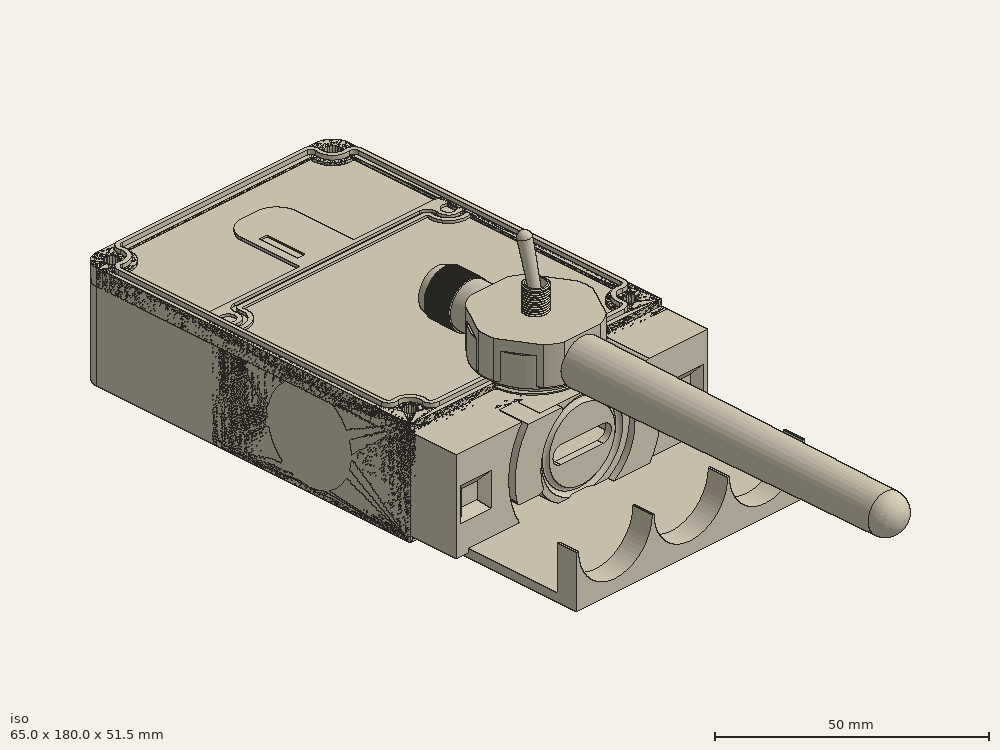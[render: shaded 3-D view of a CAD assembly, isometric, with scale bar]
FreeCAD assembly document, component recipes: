
FREECAD ASSEMBLY — COMPONENT RECIPES ("NomadShell_0.1")

This assembly document has 23 components, labeled P0..P22 below (a component is one placed body or linked part). 12 of them carry a construction recipe — the FreeCAD feature program that regenerates the part from scratch, quoted from this document or its linked companion documents; the rest are supplied as boundary geometry only. No exploded tour is included for this assembly.
NOTE — this tour is split across 2 documents so each fits a 32k-token context. This is document 1: the component sections continue in the remaining 1 document, each repeating the header above.
COMPONENT P0 — geometry summary ("Magnetic Pogo Connector 3 Pin (Type 1)007"; no construction recipe available for this part):
  bounding box: 15.0 x 5.8 x 4.0 mm
  tessellated surface: 7,316 triangles
  volume: 230 mm^3 (67% of its bounding box)
  symmetry: 2-fold rotationally symmetric about the y axis; mirror-symmetric across its x mid-plane, z mid-plane
COMPONENT P1 — geometry summary ("Magnetic Pogo Connector 3 Pin (Type 2)007"; no construction recipe available for this part):
  bounding box: 15.0 x 6.6 x 4.0 mm
  tessellated surface: 8,720 triangles
  volume: 231 mm^3 (58% of its bounding box)
  symmetry: 2-fold rotationally symmetric about the y axis; mirror-symmetric across its x mid-plane, z mid-plane
COMPONENT P2 — geometry summary ("RAK19003 (Solid)001"; no construction recipe available for this part):
  bounding box: 35.8 x 30.0 x 9.4 mm
  tessellated surface: 61,364 triangles
  volume: 1256 mm^3 (12% of its bounding box)
COMPONENT P3 — geometry summary ("RAK4631 (Solid)001"; no construction recipe available for this part):
  bounding box: 30.0 x 20.0 x 4.4 mm
  tessellated surface: 23,072 triangles
  volume: 875 mm^3 (33% of its bounding box)
COMPONENT P4 — geometry summary ("sma001"; no construction recipe available for this part):
  bounding box: 17.0 x 10.2 x 10.2 mm
  tessellated surface: 14,722 triangles
  volume: 428 mm^3 (24% of its bounding box)
COMPONENT P5 — geometry summary ("18650 v003"; no construction recipe available for this part):
  bounding box: 65.0 x 18.0 x 18.0 mm
  tessellated surface: 12,208 triangles
  volume: 16488 mm^3 (78% of its bounding box)
  symmetry: 2-fold rotationally symmetric about the x axis; revolution-symmetric about the y axis through its bounding-box center; 2-fold rotationally symmetric about the z axis; mirror-symmetric across its x mid-plane, y mid-plane, z mid-plane
COMPONENT P6 — geometry summary ("18650 v002"; no construction recipe available for this part):
  bounding box: 65.0 x 18.0 x 18.0 mm
  tessellated surface: 12,208 triangles
  volume: 16488 mm^3 (78% of its bounding box)
  symmetry: 2-fold rotationally symmetric about the x axis; revolution-symmetric about the y axis through its bounding-box center; 2-fold rotationally symmetric about the z axis; mirror-symmetric across its x mid-plane, y mid-plane, z mid-plane
COMPONENT P7 — geometry summary ("antenna_WiFi_RP-SMA_conn v003"; no construction recipe available for this part):
  bounding box: 120.4 x 11.1 x 11.0 mm
  tessellated surface: 27,859 triangles
  volume: 5611 mm^3 (38% of its bounding box)
  symmetry: mirror-symmetric across its x mid-plane
COMPONENT P8 — recipe-attached ("base001", modeled in this document).
Construction recipe (the document's own serialized feature program — sketch geometry with constraints, then the solid features built on it; lengths are millimeters unless a unit is written):

FEATURE [Sketcher::SketchObject] Sketch013  label="main_luge"
  ArcFitTolerance = 1e-06
  AttachmentSupport = -> [XZ_Plane066]
  ExternalTypes = [0]
  FullyConstrained = true
  MakeInternals = false
  MapMode = 5
  Placement = pos=(0,0,0) rot=(1,0,0;1.5708rad)
  expr: Constraints[10] = VarSet.case_height
  expr: Constraints[12] = VarSet.case_height / 2
  expr: Constraints[17] = VarSet.Base_connector_bounting_box_height
  expr: Constraints[29] = VarSet.Base_connector_external_lug
  expr: Constraints[34] = VarSet.Base_connector_external_lug
  expr: Constraints[48] = VarSet.Base_connector_internal_lug
  expr: Constraints[50] = VarSet.Base_connector_internal_lug
  expr: Constraints[52] = VarSet.Base_connector_lug_remaining_key
  expr: Constraints[53] = VarSet.Base_connector_lug_remaining_key
  expr: Constraints[9] = VarSet.base_width
  sketch-geometry (20):
    g0: LineSegment [constr] StartX=-32.5 StartY=0 StartZ=0 EndX=-32.5 EndY=-25 EndZ=0
    g1: LineSegment [constr] StartX=-32.5 StartY=-25 StartZ=0 EndX=32.5 EndY=-25 EndZ=0
    g2: LineSegment [constr] StartX=32.5 StartY=-25 StartZ=0 EndX=32.5 EndY=0 EndZ=0
    g3: LineSegment [constr] StartX=32.5 StartY=0 StartZ=0 EndX=-32.5 EndY=0 EndZ=0
    g4: GeomPoint X=0 Y=-12.5 Z=0
    g5: LineSegment [constr] StartX=-32.5 StartY=-1.5 StartZ=0 EndX=32.5 EndY=-1.5 EndZ=0
    g6: LineSegment [constr] StartX=-32.5 StartY=-23.5 StartZ=0 EndX=32.5 EndY=-23.5 EndZ=0
    g7: LineSegment [constr] StartX=-32.5 StartY=-1.5 StartZ=0 EndX=32.5 EndY=-23.5 EndZ=0
    g8: ArcOfCircle CenterX=0 CenterY=-12.5 CenterZ=0 NormalX=0 NormalY=0 NormalZ=1 AngleXU=0 Radius=12 StartAngle=5.85341 EndAngle=7.44284
    g9: ArcOfCircle CenterX=0 CenterY=-12.5 CenterZ=0 NormalX=0 NormalY=0 NormalZ=1 AngleXU=0 Radius=19 StartAngle=6.01689 EndAngle=6.90062
    g10: LineSegment StartX=10.9087 StartY=-17.5 StartZ=0 EndX=18.3303 EndY=-17.5 EndZ=0
    g11: LineSegment StartX=4.79583 StartY=-1.5 StartZ=0 EndX=15.4919 EndY=-1.5 EndZ=0
    g12: ArcOfCircle CenterX=0 CenterY=-12.5 CenterZ=0 NormalX=0 NormalY=0 NormalZ=1 AngleXU=0 Radius=12 StartAngle=2.71182 EndAngle=4.30125
    g13: ArcOfCircle CenterX=0 CenterY=-12.5 CenterZ=0 NormalX=0 NormalY=0 NormalZ=1 AngleXU=0 Radius=19 StartAngle=2.8753 EndAngle=3.75903
    g14: LineSegment StartX=-18.3303 StartY=-7.5 StartZ=0 EndX=-10.9087 EndY=-7.5 EndZ=0
    g15: LineSegment StartX=-15.4919 StartY=-23.5 StartZ=0 EndX=-4.79583 EndY=-23.5 EndZ=0
    g16: LineSegment StartX=-32.5 StartY=-1.5 StartZ=0 EndX=-32.5 EndY=-23.5 EndZ=0
    g17: LineSegment StartX=-32.5 StartY=-23.5 StartZ=0 EndX=32.5 EndY=-23.5 EndZ=0
    g18: LineSegment StartX=32.5 StartY=-23.5 StartZ=0 EndX=32.5 EndY=-1.5 EndZ=0
    g19: LineSegment StartX=32.5 StartY=-1.5 StartZ=0 EndX=-32.5 EndY=-1.5 EndZ=0
  constraints (56):
    c: Coincident(g0,g1)
    c: Coincident(g1,g2)
    c: Coincident(g2,g3)
    c: Coincident(g3,g0)
    c: Vertical(g0)
    c: Vertical(g2)
    c: Horizontal(g1)
    c: PointOnObject(g0,g-1)
    c: Symmetric(g0,g2,g-2)
    c: DistanceX(g0,g2) = 65
    c: DistanceY(g0,g-1) = 25
    c: PointOnObject(g4,g-2)
    c: DistanceY(g4,g-1) = 12.5
    c: PointOnObject(g6,g0)
    c: Horizontal(g6)
    c: PointOnObject(g6,g2)
    c: PointOnObject(g5,g2)
    c: DistanceY(g6,g5) = 22
    c: PointOnObject(g5,g0)
    c: Parallel(g5,g3)
    c: Coincident(g7,g5)
    c: Coincident(g7,g6)
    c: PointOnObject(g4,g7)
    c: Coincident(g8,g4)
    c: Coincident(g9,g4)
    c: Coincident(g10,g8)
    c: Coincident(g10,g9)
    c: Coincident(g9,g11)
    c: Parallel(g11,g3)
    c: Radius(g9) = 19
    c: Coincident(g12,g4)
    c: Coincident(g13,g4)
    c: Coincident(g14,g13)
    c: Coincident(g14,g12)
    c: Radius(g13) = 19
    c: Coincident(g15,g13)
    c: Parallel(g15,g5)
    c: Coincident(g16,g17)
    c: Coincident(g17,g18)
    c: Coincident(g18,g19)
    c: Coincident(g19,g16)
    c: Vertical(g16)
    c: Horizontal(g17)
    c: Symmetric(g16,g18,g-2)
    c: Parallel(g10,g5)
    c: Parallel(g14,g5)
    c: Coincident(g16,g5)
    c: Coincident(g17,g6)
    c: Radius(g12) = 12
    c: PointOnObject(g12,g6)
    c: Radius(g8) = 12
    c: PointOnObject(g8,g5)
    c: Distance(g9,g17) = 6
    c: Distance(g12,g19) = 6
    c: Coincident(g11,g8)
    c: Coincident(g15,g12)
FEATURE [Sketcher::SketchObject] Sketch014
  ArcFitTolerance = 1e-06
  AttachmentSupport = -> [XZ_Plane066]
  ExternalTypes = [0]
  FullyConstrained = true
  MakeInternals = false
  MapMode = 5
  Placement = pos=(0,0,0) rot=(1,0,0;1.5708rad)
  expr: Constraints[11] = VarSet.Base_connector_bounting_box_height
  expr: Constraints[18] = (VarSet.Base_connector_external_lug + VarSet.Base_connector_internal_lug) / 2
  expr: Constraints[19] = (VarSet.Base_connector_external_lug + VarSet.Base_connector_internal_lug) / 2
  expr: Constraints[24] = VarSet.Base_connector_internal_lug
  expr: Constraints[28] = VarSet.Base_connector_internal_lug
  expr: Constraints[36] = VarSet.Base_connector_bounting_box_height - VarSet.Base_connector_height_lug
  expr: Constraints[38] = VarSet.Base_connector_bounting_box_height - VarSet.Base_connector_height_lug
  expr: Constraints[3] = VarSet.base_width
  expr: Constraints[6] = VarSet.case_height / 2
  sketch-geometry (14):
    g0: LineSegment [constr] StartX=-32.5 StartY=-1.5 StartZ=0 EndX=-32.5 EndY=-23.5 EndZ=0
    g1: LineSegment [constr] StartX=-32.5 StartY=-23.5 StartZ=0 EndX=32.5 EndY=-23.5 EndZ=0
    g2: LineSegment [constr] StartX=32.5 StartY=-23.5 StartZ=0 EndX=32.5 EndY=-1.5 EndZ=0
    g3: GeomPoint X=0 Y=-12.5 Z=0
    g4: LineSegment [constr] StartX=-32.5 StartY=-12.5 StartZ=0 EndX=32.5 EndY=-12.5 EndZ=0
    g5: LineSegment StartX=11.9583 StartY=-13.5 StartZ=0 EndX=15.4677 EndY=-13.5 EndZ=0
    g6: LineSegment [constr] StartX=-32.5 StartY=-1.5 StartZ=0 EndX=32.5 EndY=-1.5 EndZ=0
    g7: ArcOfCircle CenterX=0 CenterY=-12.5 CenterZ=0 NormalX=0 NormalY=0 NormalZ=1 AngleXU=0 Radius=15.5 StartAngle=6.21862 EndAngle=7.07223
    g8: ArcOfCircle CenterX=-1.6e-15 CenterY=-12.5 CenterZ=0 NormalX=0 NormalY=0 NormalZ=1 AngleXU=0 Radius=15.5 StartAngle=3.07703 EndAngle=3.93063
    g9: LineSegment StartX=-15.4677 StartY=-11.5 StartZ=0 EndX=-11.9583 EndY=-11.5 EndZ=0
    g10: ArcOfCircle CenterX=-1.6e-15 CenterY=-12.5 CenterZ=0 NormalX=0 NormalY=0 NormalZ=1 AngleXU=0 Radius=12 StartAngle=3.05816 EndAngle=4.30125
    g11: LineSegment StartX=-4.79583 StartY=-23.5 StartZ=0 EndX=-10.9202 EndY=-23.5 EndZ=0
    g12: ArcOfCircle CenterX=0 CenterY=-12.5 CenterZ=0 NormalX=0 NormalY=0 NormalZ=1 AngleXU=0 Radius=12 StartAngle=6.19976 EndAngle=7.44284
    g13: LineSegment StartX=4.79583 StartY=-1.5 StartZ=0 EndX=10.9202 EndY=-1.5 EndZ=0
  constraints (39):
    c: Vertical(g0)
    c: Vertical(g2)
    c: Horizontal(g1)
    c: DistanceX(g0,g2) = 65
    c: Symmetric(g0,g2,g-2)
    c: PointOnObject(g3,g-2)
    c: DistanceY(g3,g-1) = 12.5
    c: Symmetric(g0,g0,g4)
    c: Symmetric(g2,g2,g4)
    c: Coincident(g1,g2)
    c: Coincident(g1,g0)
    c: DistanceY(g1,g2) = 22
    c: Coincident(g6,g0)
    c: Coincident(g6,g2)
    c: PointOnObject(g3,g4)
    c: Coincident(g7,g3)
    c: Coincident(g7,g5)
    c: Symmetric(g4,g4,g8)
    c: Radius(g7) = 15.5
    c: Radius(g8) = 15.5
    c: Coincident(g8,g9)
    c: Coincident(g10,g8)
    c: Coincident(g10,g9)
    c: Coincident(g11,g10)
    c: Radius(g10) = 12
    c: Coincident(g8,g11)
    c: Coincident(g12,g3)
    c: Coincident(g12,g5)
    c: Radius(g12) = 12
    c: Coincident(g13,g12)
    c: Coincident(g13,g7)
    c: Parallel(g9,g6)
    c: Parallel(g1,g5)
    c: Parallel(g11,g1)
    c: Parallel(g13,g1)
    c: PointOnObject(g10,g1)
    c: Distance(g8,g6) = 10
    c: PointOnObject(g7,g6)
    c: Distance(g5,g1) = 10
FEATURE [PartDesign::Pad] Pad010
  Direction = (0,-1,2e-16)
  Length = 12
  Length2 = 10
  Placement = pos=(0,0,0) rot=(1,0,0;1.5708rad)
  Profile = -> Sketch013 [Edge9,Edge12,Edge10,Edge11]
  ReferenceAxis = -> Sketch013 [N_Axis]
  Refine = true
  Suppressed = false
  Type = 0
  expr: Length = VarSet.Base_connector_height_lug
FEATURE [PartDesign::Pocket] Pocket021
  BaseFeature = -> Pad010
  Direction = (0,1,-2e-16)
  Length = 6.2
  Length2 = 5
  Placement = pos=(0,0,0) rot=(1,0,0;1.5708rad)
  Profile = -> Sketch013 [Edge7,Edge8,Edge6,Edge5,Edge3,Edge2,Edge4,Edge1]
  ReferenceAxis = -> Sketch013 [N_Axis]
  Refine = true
  Reversed = true
  Suppressed = false
  Type = 0
  expr: Length = VarSet.Base_connector_height_lug / 2 + VarSet.Base_connector_oring_offset
FEATURE [Sketcher::SketchObject] Sketch016
  ArcFitTolerance = 1e-06
  AttachmentSupport = -> [Pocket021]
  ExternalTypes = [0]
  FullyConstrained = false
  MakeInternals = false
  MapMode = 5
  Placement = pos=(0,-12,0) rot=(1,0,0;1.5708rad)
  expr: Constraints[11] = VarSet.Base_connector_bounting_box_height
  expr: Constraints[17] = VarSet.Base_connector_external_lug
  expr: Constraints[18] = 19
  expr: Constraints[20] = VarSet.Base_connector_internal_lug
  expr: Constraints[28] = (VarSet.Base_connector_external_lug + VarSet.Base_connector_internal_lug) / 2
  expr: Constraints[39] = VarSet.Base_connector_lug_remaining_key
  expr: Constraints[3] = VarSet.base_width
  expr: Constraints[47] = (VarSet.Base_connector_external_lug + VarSet.Base_connector_internal_lug) / 2
  expr: Constraints[48] = VarSet.Base_connector_internal_lug
  expr: Constraints[54] = VarSet.Base_connector_lug_remaining_key
  expr: Constraints[6] = VarSet.case_height / 2
  sketch-geometry (20):
    g0: LineSegment [constr] StartX=-32.5 StartY=-1.5 StartZ=0 EndX=-32.5 EndY=-23.5 EndZ=0
    g1: LineSegment [constr] StartX=-32.5 StartY=-23.5 StartZ=0 EndX=32.5 EndY=-23.5 EndZ=0
    g2: LineSegment [constr] StartX=32.5 StartY=-23.5 StartZ=0 EndX=32.5 EndY=-1.5 EndZ=0
    g3: GeomPoint X=0 Y=-12.5 Z=0
    g4: LineSegment [constr] StartX=-32.5 StartY=-12.5 StartZ=0 EndX=32.5 EndY=-12.5 EndZ=0
    g5: LineSegment [constr] StartX=-32.5 StartY=-1.5 StartZ=0 EndX=32.5 EndY=-1.5 EndZ=0
    g6: ArcOfCircle CenterX=0 CenterY=-12.5 CenterZ=0 NormalX=0 NormalY=0 NormalZ=1 AngleXU=0 Radius=19 StartAngle=5.66575 EndAngle=6.90062
    g7: ArcOfCircle CenterX=-3e-16 CenterY=-12.5 CenterZ=0 NormalX=0 NormalY=0 NormalZ=1 AngleXU=0 Radius=19 StartAngle=2.52416 EndAngle=3.75903
    g8: ArcOfCircle CenterX=0 CenterY=-12.5 CenterZ=0 NormalX=0 NormalY=0 NormalZ=1 AngleXU=0 Radius=12 StartAngle=0.429775 EndAngle=1.15966
    g9: ArcOfCircle CenterX=0 CenterY=-12.5 CenterZ=0 NormalX=0 NormalY=0 NormalZ=1 AngleXU=0 Radius=15.5 StartAngle=5.49415 EndAngle=6.61164
    g10: LineSegment [constr] StartX=-15.4919 StartY=-1.5 StartZ=0 EndX=-4.79582 EndY=-1.5 EndZ=0
    g11: LineSegment [constr] StartX=-13.0749 StartY=-23.5 StartZ=0 EndX=-4.79583 EndY=-23.5 EndZ=0
    g12: LineSegment StartX=15.4919 StartY=-1.5 StartZ=0 EndX=4.79583 EndY=-1.5 EndZ=0
    g13: LineSegment StartX=15.4919 StartY=-23.5 StartZ=0 EndX=10.9202 EndY=-23.5 EndZ=0
    g14: LineSegment StartX=14.6714 StartY=-7.5 StartZ=0 EndX=10.9087 EndY=-7.5 EndZ=0
    g15: LineSegment StartX=-15.4919 StartY=-23.5 StartZ=0 EndX=-4.79583 EndY=-23.5 EndZ=0
    g16: LineSegment StartX=-10.9202 StartY=-1.5 StartZ=0 EndX=-15.4919 EndY=-1.5 EndZ=0
    g17: LineSegment StartX=-14.6714 StartY=-17.5 StartZ=0 EndX=-10.9087 EndY=-17.5 EndZ=0
    g18: ArcOfCircle CenterX=-3e-16 CenterY=-12.5 CenterZ=0 NormalX=0 NormalY=0 NormalZ=1 AngleXU=0 Radius=15.5 StartAngle=2.35255 EndAngle=3.47005
    g19: ArcOfCircle CenterX=0 CenterY=-12.5 CenterZ=0 NormalX=0 NormalY=0 NormalZ=1 AngleXU=0 Radius=12 StartAngle=3.57137 EndAngle=4.30125
  constraints (55):
    c: Vertical(g0)
    c: Vertical(g2)
    c: Horizontal(g1)
    c: DistanceX(g0,g2) = 65
    c: Symmetric(g0,g2,g-2)
    c: PointOnObject(g3,g-2)
    c: DistanceY(g3,g-1) = 12.5
    c: Symmetric(g0,g0,g4)
    c: Symmetric(g2,g2,g4)
    c: Coincident(g1,g2)
    c: Coincident(g1,g0)
    c: DistanceY(g1,g2) = 22
    c: Coincident(g5,g0)
    c: Coincident(g5,g2)
    c: PointOnObject(g3,g4)
    c: Coincident(g6,g3)
    c: Symmetric(g4,g4,g7)
    c: Radius(g6) = 19
    c: Radius(g7) = 19
    c: Coincident(g8,g3)
    c: Radius(g8) = 12
    c: Coincident(g9,g3)
    c: PointOnObject(g8,g5)
    c: PointOnObject(g10,g5)
    c: PointOnObject(g11,g1)
    c: PointOnObject(g7,g5)
    c: Coincident(g10,g7)
    c: PointOnObject(g11,g1)
    c: Radius(g9) = 15.5
    c: PointOnObject(g6,g5)
    c: Coincident(g12,g6)
    c: Coincident(g12,g8)
    c: PointOnObject(g6,g1)
    c: Coincident(g13,g9)
    c: Horizontal(g13)
    c: Coincident(g14,g9)
    c: Parallel(g14,g5)
    c: Coincident(g14,g8)
    c: Coincident(g13,g6)
    c: Distance(g8,g5) = 6
    c: Coincident(g16,g7)
    c: Horizontal(g17)
    c: PointOnObject(g16,g5)
    c: Coincident(g18,g7)
    c: Coincident(g18,g16)
    c: Coincident(g19,g3)
    c: Coincident(g19,g15)
    c: Radius(g18) = 15.5
    c: Radius(g19) = 12
    c: Coincident(g17,g19)
    c: Coincident(g17,g18)
    c: Coincident(g7,g15)
    c: PointOnObject(g7,g1)
    c: PointOnObject(g15,g1)
    c: Distance(g7,g17) = 6
FEATURE [PartDesign::Pocket] Pocket022
  BaseFeature = -> Pocket021
  Direction = (0,1,-2e-16)
  Length = 6
  Length2 = 5
  Placement = pos=(0,0,0) rot=(1,0,0;1.5708rad)
  Profile = -> Sketch016
  ReferenceAxis = -> Sketch016 [N_Axis]
  Refine = true
  Suppressed = false
  Type = 0
  expr: Length = VarSet.Base_connector_height_lug / 2
FEATURE [Sketcher::SketchObject] Sketch017  label="pogo_pins001"
  ArcFitTolerance = 1e-06
  AttachmentSupport = -> [Pocket022]
  ExternalTypes = [0]
  FullyConstrained = true
  MakeInternals = false
  MapMode = 5
  Placement = pos=(0,-12,0) rot=(1,0,0;1.5708rad)
  expr: Constraints[12] = VarSet.Base_pogopins_r
  expr: Constraints[1] = VarSet.case_height / 2
  expr: Constraints[25] = VarSet.Base_pogoping_lenght
  sketch-geometry (11):
    g0: GeomPoint X=0 Y=-12.5 Z=0
    g1: ArcOfCircle CenterX=-5.45 CenterY=-12.5 CenterZ=0 NormalX=0 NormalY=0 NormalZ=1 AngleXU=0 Radius=2.1 StartAngle=1.5708 EndAngle=4.71239
    g2: ArcOfCircle CenterX=5.45 CenterY=-12.5 CenterZ=0 NormalX=0 NormalY=0 NormalZ=1 AngleXU=0 Radius=2.1 StartAngle=4.71239 EndAngle=7.85398
    g3: LineSegment StartX=-5.45 StartY=-10.4 StartZ=0 EndX=5.45 EndY=-10.4 EndZ=0
    g4: LineSegment StartX=-5.45 StartY=-14.6 StartZ=0 EndX=5.45 EndY=-14.6 EndZ=0
    g5: LineSegment [constr] StartX=-5.45 StartY=-12.5 StartZ=0 EndX=5.45 EndY=-12.5 EndZ=0
    g6: GeomPoint [constr] X=0 Y=-12.5 Z=0
    g7: LineSegment [constr] StartX=-7.55 StartY=-10.4 StartZ=0 EndX=-7.55 EndY=-14.6 EndZ=0
    g8: LineSegment [constr] StartX=-7.55 StartY=-14.6 StartZ=0 EndX=7.55 EndY=-14.6 EndZ=0
    g9: LineSegment [constr] StartX=7.55 StartY=-14.6 StartZ=0 EndX=7.55 EndY=-10.4 EndZ=0
    g10: LineSegment [constr] StartX=7.55 StartY=-10.4 StartZ=0 EndX=-7.55 EndY=-10.4 EndZ=0
  constraints (26):
    c: PointOnObject(g0,g-2)
    c: Distance(g0,g-1) = 12.5
    c: Tangent(g1,g3) = 1.5708
    c: Tangent(g1,g4) = -1.5708
    c: Tangent(g2,g3) = 1.5708
    c: Tangent(g2,g4) = -1.5708
    c: Equal(g1,g2)
    c: Horizontal(g3)
    c: Coincident(g5,g1)
    c: Coincident(g5,g2)
    c: Symmetric(g5,g5,g6)
    c: Coincident(g0,g6)
    c: Radius(g1) = 2.1
    c: Coincident(g7,g8)
    c: Coincident(g8,g9)
    c: Coincident(g9,g10)
    c: Coincident(g10,g7)
    c: Vertical(g7)
    c: Vertical(g9)
    c: Horizontal(g8)
    c: Horizontal(g10)
    c: PointOnObject(g2,g10)
    c: PointOnObject(g2,g8)
    c: Tangent(g2,g9)
    c: Tangent(g7,g1)
    c: DistanceX(g7,g9) = 15.1
FEATURE [PartDesign::Pocket] Pocket023  label="pogo_pins002"
  BaseFeature = -> Pocket022
  Direction = (0,1,-2e-16)
  Length = 1.5
  Length2 = 5
  Placement = pos=(0,0,0) rot=(1,0,0;1.5708rad)
  Profile = -> Sketch017
  ReferenceAxis = -> Sketch017 [N_Axis]
  Refine = true
  Suppressed = false
  Type = 0
  expr: Length = VarSet.Base_pogopin_cutout_height
FEATURE [Sketcher::SketchObject] Sketch023  label="pogo_pins_outside"
  ArcFitTolerance = 1e-06
  AttachmentSupport = -> [XZ_Plane066]
  ExternalTypes = [0]
  FullyConstrained = true
  MakeInternals = false
  MapMode = 5
  Placement = pos=(0,0,0) rot=(1,0,0;1.5708rad)
  expr: Constraints[12] = VarSet.Base_pogopin_outside
  expr: Constraints[13] = VarSet.Base_pogopins_r * 3
  expr: Constraints[1] = VarSet.case_height / 2
  sketch-geometry (6):
    g0: GeomPoint X=0 Y=-12.5 Z=0
    g1: LineSegment StartX=-10.5 StartY=-9.35 StartZ=0 EndX=-10.5 EndY=-15.65 EndZ=0
    g2: LineSegment StartX=-10.5 StartY=-15.65 StartZ=0 EndX=10.5 EndY=-15.65 EndZ=0
    g3: LineSegment StartX=10.5 StartY=-15.65 StartZ=0 EndX=10.5 EndY=-9.35 EndZ=0
    g4: LineSegment StartX=10.5 StartY=-9.35 StartZ=0 EndX=-10.5 EndY=-9.35 EndZ=0
    g5: GeomPoint [constr] X=0 Y=-12.5 Z=0
  constraints (14):
    c: PointOnObject(g0,g-2)
    c: DistanceY(g0,g-1) = 12.5
    c: Coincident(g1,g2)
    c: Coincident(g2,g3)
    c: Coincident(g3,g4)
    c: Coincident(g4,g1)
    c: Vertical(g1)
    c: Vertical(g3)
    c: Horizontal(g2)
    c: Horizontal(g4)
    c: Symmetric(g3,g1,g5)
    c: Coincident(g5,g0)
    c: Distance(g1,g3) = 21
    c: DistanceY(g2,g3) = 6.3
FEATURE [PartDesign::Pocket] Pocket024  label="pogo_pins_outside001"
  BaseFeature = -> Pocket023
  Direction = (0,1,-2e-16)
  Length = 10.5
  Length2 = 5
  Placement = pos=(0,0,0) rot=(1,0,0;1.5708rad)
  Profile = -> Sketch023
  ReferenceAxis = -> Sketch023 [N_Axis]
  Refine = true
  Reversed = true
  Suppressed = false
  Type = 0
  expr: Length = VarSet.Base_connector_height_lug - VarSet.Base_pogopin_cutout_height
FEATURE [PartDesign::Fillet] Fillet
  Base = -> Pocket024 [Edge5,Edge60]
  BaseFeature = -> Pocket024
  Placement = pos=(0,0,0) rot=(1,0,0;1.5708rad)
  Radius = 10
  Refine = true
  SupportTransform = false
  Suppressed = false
  UseAllEdges = false
FEATURE [Sketcher::SketchObject] Sketch  label="main_diamention"
  ArcFitTolerance = 1e-06
  AttachmentSupport = -> [XY_Plane053]
  ExternalTypes = [0]
  FullyConstrained = true
  MakeInternals = false
  MapMode = 5
  expr: Constraints[13] = VarSet.base_width
  expr: Constraints[14] = VarSet.Base_base_lenght
  expr: Constraints[30] = VarSet.Base_m3_insert
  expr: Constraints[45] = VarSet.Base_case_thickness
  expr: Constraints[46] = VarSet.Base_case_thickness
  expr: Constraints[47] = VarSet.Base_case_thickness
  expr: Constraints[50] = VarSet.Base_case_thickness + VarSet.Base_m3_insert / 2
  expr: Constraints[51] = VarSet.Base_case_thickness + VarSet.Base_m3_insert / 2
  expr: Constraints[52] = VarSet.Base_case_thickness + VarSet.Base_m3_insert / 2
  expr: Constraints[71] = VarSet.Base_case_thickness / 2
  expr: Constraints[72] = VarSet.Base_case_thickness / 2
  expr: Constraints[73] = VarSet.Base_case_thickness / 2
  expr: Constraints[84] = VarSet.Base_case_thickness / 2
  expr: Constraints[86] = VarSet.Base_case_thickness + VarSet.Base_m3_insert / 2
  expr: Constraints[92] = VarSet.Base_case_thickness
  sketch-geometry (40):
    g0: LineSegment StartX=-32.5 StartY=0 StartZ=0 EndX=32.5 EndY=0 EndZ=0
    g1: LineSegment StartX=32.5 StartY=0 StartZ=0 EndX=32.5 EndY=51 EndZ=0
    g2: LineSegment StartX=28.5 StartY=55 StartZ=0 EndX=-28.5 EndY=55 EndZ=0
    g3: LineSegment StartX=-32.5 StartY=51 StartZ=0 EndX=-32.5 EndY=0 EndZ=0
    g4: GeomPoint [constr] X=-32.5 Y=55 Z=0
    g5: ArcOfCircle CenterX=28.5 CenterY=51 CenterZ=0 NormalX=0 NormalY=0 NormalZ=1 AngleXU=0 Radius=4 StartAngle=0 EndAngle=1.5708
    g6: GeomPoint [constr] X=32.5 Y=55 Z=0
    g7: Circle CenterX=-28.5 CenterY=4 CenterZ=0 NormalX=0 NormalY=0 NormalZ=1 AngleXU=0 Radius=1.6
    g8: Circle CenterX=28.5 CenterY=4 CenterZ=0 NormalX=0 NormalY=0 NormalZ=1 AngleXU=0 Radius=1.6
    g9: Circle CenterX=28.5 CenterY=51 CenterZ=0 NormalX=0 NormalY=0 NormalZ=1 AngleXU=0 Radius=1.6
    g10: Circle CenterX=-28.5 CenterY=51 CenterZ=0 NormalX=0 NormalY=0 NormalZ=1 AngleXU=0 Radius=1.6
    g11: LineSegment [constr] StartX=-28.5 StartY=51 StartZ=0 EndX=-28.5 EndY=4 EndZ=0
    g12: LineSegment [constr] StartX=-28.5 StartY=4 StartZ=0 EndX=28.5 EndY=4 EndZ=0
    g13: LineSegment [constr] StartX=28.5 StartY=4 StartZ=0 EndX=28.5 EndY=51 EndZ=0
    g14: LineSegment [constr] StartX=28.5 StartY=51 StartZ=0 EndX=-28.5 EndY=51 EndZ=0
    g15: LineSegment StartX=-24.01 StartY=52 StartZ=0 EndX=24.01 EndY=52 EndZ=0
    g16: LineSegment StartX=29.5 StartY=46.51 StartZ=0 EndX=29.5 EndY=8.48999 EndZ=0
    g17: LineSegment StartX=24.01 StartY=3 StartZ=0 EndX=-24.01 EndY=3 EndZ=0
    g18: LineSegment StartX=-29.5 StartY=8.48999 StartZ=0 EndX=-29.5 EndY=46.51 EndZ=0
    g19: ArcOfCircle CenterX=-28.5 CenterY=4 CenterZ=0 NormalX=0 NormalY=0 NormalZ=1 AngleXU=0 Radius=4.6 StartAngle=6.06404 EndAngle=8.07312
    g20: ArcOfCircle CenterX=-28.5 CenterY=51 CenterZ=0 NormalX=0 NormalY=0 NormalZ=1 AngleXU=0 Radius=4.6 StartAngle=4.49325 EndAngle=6.50233
    g21: ArcOfCircle CenterX=28.5 CenterY=51 CenterZ=0 NormalX=0 NormalY=0 NormalZ=1 AngleXU=0 Radius=4.6 StartAngle=2.92245 EndAngle=4.93153
    g22: ArcOfCircle CenterX=28.5 CenterY=4 CenterZ=0 NormalX=0 NormalY=0 NormalZ=1 AngleXU=0 Radius=4.6 StartAngle=1.35166 EndAngle=3.36073
    g23: ArcOfCircle CenterX=28.5 CenterY=4 CenterZ=0 NormalX=0 NormalY=0 NormalZ=1 AngleXU=0 Radius=3.1 StartAngle=1.35166 EndAngle=3.36073
    g24: ArcOfCircle CenterX=24.01 CenterY=3 CenterZ=0 NormalX=0 NormalY=0 NormalZ=1 AngleXU=-3.14159 Radius=1.5 StartAngle=1.5708 EndAngle=3.36073
    g25: LineSegment StartX=24.01 StartY=1.5 StartZ=0 EndX=-24.01 EndY=1.5 EndZ=0
    g26: ArcOfCircle CenterX=-24.01 CenterY=3 CenterZ=0 NormalX=0 NormalY=0 NormalZ=1 AngleXU=1.55119 Radius=1.5 StartAngle=1.37126 EndAngle=3.1612
    g27: ArcOfCircle CenterX=-28.5 CenterY=4 CenterZ=0 NormalX=0 NormalY=0 NormalZ=1 AngleXU=0 Radius=3.1 StartAngle=6.06404 EndAngle=8.07312
    g28: ArcOfCircle CenterX=-29.5 CenterY=8.48999 CenterZ=0 NormalX=0 NormalY=0 NormalZ=1 AngleXU=1.5708 Radius=1.5 StartAngle=1.5708 EndAngle=3.36073
    g29: LineSegment StartX=-31 StartY=8.48999 StartZ=0 EndX=-31 EndY=46.51 EndZ=0
    g30: ArcOfCircle CenterX=-29.5 CenterY=46.51 CenterZ=0 NormalX=0 NormalY=0 NormalZ=1 AngleXU=-0.0196091 Radius=1.5 StartAngle=1.37126 EndAngle=3.1612
    g31: ArcOfCircle CenterX=-28.5 CenterY=51 CenterZ=0 NormalX=0 NormalY=0 NormalZ=1 AngleXU=0 Radius=3.1 StartAngle=4.49325 EndAngle=6.50233
    g32: ArcOfCircle CenterX=-24.01 CenterY=52 CenterZ=0 NormalX=0 NormalY=0 NormalZ=1 AngleXU=0 Radius=1.5 StartAngle=1.5708 EndAngle=3.36073
    g33: LineSegment StartX=-24.01 StartY=53.5 StartZ=0 EndX=24.01 EndY=53.5 EndZ=0
    g34: ArcOfCircle CenterX=24.01 CenterY=52 CenterZ=0 NormalX=0 NormalY=0 NormalZ=1 AngleXU=-1.5708 Radius=1.5 StartAngle=1.35166 EndAngle=3.14159
    g35: ArcOfCircle CenterX=28.5 CenterY=51 CenterZ=0 NormalX=0 NormalY=0 NormalZ=1 AngleXU=0 Radius=3.1 StartAngle=2.92245 EndAngle=4.93153
    g36: ArcOfCircle CenterX=29.5 CenterY=46.51 CenterZ=0 NormalX=0 NormalY=0 NormalZ=1 AngleXU=-1.5708 Radius=1.5 StartAngle=1.5708 EndAngle=3.36073
    g37: LineSegment StartX=31 StartY=46.51 StartZ=0 EndX=31 EndY=8.48999 EndZ=0
    g38: ArcOfCircle CenterX=29.5 CenterY=8.48999 CenterZ=0 NormalX=0 NormalY=0 NormalZ=1 AngleXU=3.12198 Radius=1.5 StartAngle=1.37126 EndAngle=3.1612
    g39: ArcOfCircle CenterX=-28.5 CenterY=51 CenterZ=0 NormalX=0 NormalY=0 NormalZ=1 AngleXU=0 Radius=4 StartAngle=1.5708 EndAngle=3.14159
  constraints (94):
    c: Coincident(g0,g1)
    c: Coincident(g3,g0)
    c: Horizontal(g2)
    c: Vertical(g1)
    c: Vertical(g3)
    c: PointOnObject(g0,g-1)
    c: Symmetric(g0,g0,g-2)
    c: PointOnObject(g4,g3)
    c: PointOnObject(g4,g2)
    c: PointOnObject(g6,g1)
    c: PointOnObject(g6,g2)
    c: Tangent(g1,g5) = -1.5708
    c: Tangent(g2,g5) = -1.5708
    c: DistanceX(g4,g6) = 65
    c: DistanceY(g0,g4) = 55
    c: Coincident(g11,g12)
    c: Coincident(g12,g13)
    c: Coincident(g13,g14)
    c: Coincident(g14,g11)
    c: Vertical(g11)
    c: Vertical(g13)
    c: Horizontal(g12)
    c: Coincident(g11,g10)
    c: Coincident(g12,g8)
    c: Coincident(g7,g11)
    c: Coincident(g13,g9)
    c: Symmetric(g10,g9,g-2)
    c: Equal(g10,g9)
    c: Equal(g9,g8)
    c: Equal(g8,g7)
    c: Diameter(g10) = 3.2
    c: Distance(g10,g2) = 2.4
    c: Distance(g7,g0) = 2.4
    c: Horizontal(g15)
    c: Vertical(g16)
    c: Horizontal(g17)
    c: Vertical(g18)
    c: Coincident(g19,g18)
    c: Coincident(g19,g17)
    c: Coincident(g20,g18)
    c: Coincident(g20,g15)
    c: Coincident(g21,g15)
    c: Coincident(g21,g16)
    c: Coincident(g22,g16)
    c: Coincident(g22,g17)
    c: Distance(g2,g15) = 3
    c: Distance(g17,g0) = 3
    c: Distance(g1,g16) = 3
    c: Coincident(g22,g8)
    c: Coincident(g19,g7)
    c: Radius(g19) = 4.6
    c: Radius(g20) = 4.6
    c: Radius(g21) = 4.6
    c: Coincident(g10,g20)
    c: Coincident(g21,g5)
    c: Tangent(g23,g24) = 1.5708
    c: Tangent(g23,g38) = 1.5708
    c: Tangent(g24,g25) = 1.5708
    c: Tangent(g25,g26) = 1.5708
    c: Tangent(g26,g27) = 1.5708
    c: Tangent(g27,g28) = 1.5708
    c: Tangent(g28,g29) = 1.5708
    c: Tangent(g29,g30) = 1.5708
    c: Tangent(g30,g31) = 1.5708
    c: Tangent(g31,g32) = 1.5708
    c: Tangent(g32,g33) = 1.5708
    c: Tangent(g33,g34) = 1.5708
    c: Tangent(g34,g35) = 1.5708
    c: Tangent(g35,g36) = 1.5708
    c: Tangent(g36,g37) = 1.5708
    c: Tangent(g37,g38) = 1.5708
    c: Distance(g17,g25) = 1.5
    c: Distance(g37,g16) = 1.5
    c: Distance(g33,g15) = 1.5
    c: Coincident(g32,g15)
    c: Coincident(g30,g18)
    c: Coincident(g36,g16)
    c: Coincident(g24,g17)
    c: Coincident(g26,g17)
    c: Coincident(g28,g18)
    c: Coincident(g27,g7)
    c: Coincident(g23,g8)
    c: Coincident(g9,g35)
    c: Coincident(g34,g15)
    c: Distance(g27,g19) = 1.5
    c: Coincident(g38,g16)
    c: Radius(g22) = 4.6
    c: Coincident(g39,g10)
    c: Coincident(g39,g3)
    c: Tangent(g39,g2) = -1.5708
    c: Coincident(g31,g10)
    c: Coincident(g5,g9)
    c: Distance(g18,g3) = 3
    c: Distance(g7,g3) = 4
FEATURE [PartDesign::Pad] Pad
  Direction = (0,0,1)
  Length = 25
  Length2 = 10
  Profile = -> Sketch [Edge1,Edge6,Edge5,Edge4,Edge3,Edge2]
  ReferenceAxis = -> Sketch [N_Axis]
  Refine = true
  Reversed = true
  Suppressed = false
  Type = 0
  expr: Length = VarSet.case_height
FEATURE [PartDesign::Pocket] Pocket  label="body_inside"
  BaseFeature = -> Pad
  Direction = (0,0,-1)
  Length = 22
  Length2 = 5
  Profile = -> Sketch [Edge15,Edge16,Edge17,Edge18,Edge11,Edge12,Edge13,Edge14]
  ReferenceAxis = -> Sketch [N_Axis]
  Refine = true
  Suppressed = false
  Type = 0
  expr: Length = VarSet.case_height - VarSet.Base_case_thickness
FEATURE [PartDesign::Pocket] Pocket001  label="screw"
  BaseFeature = -> Pocket
  Direction = (0,0,-1)
  Length = 5
  Length2 = 5
  Midplane = true
  Profile = -> Sketch [Edge10,Edge9,Edge8,Edge7]
  ReferenceAxis = -> Sketch [N_Axis]
  Refine = true
  Suppressed = false
  Type = 1
FEATURE [Sketcher::SketchObject] Sketch003  label="pcb_standoff001"
  ArcFitTolerance = 1e-06
  AttachmentSupport = -> [Pocket001]
  ExternalGeometry = -> [Sketch]
  ExternalTypes = [0,0,0,0]
  FullyConstrained = true
  MakeInternals = false
  MapMode = 5
  Placement = pos=(0,0,-22) rot=(0,0,1;0rad)
  sketch-geometry (10):
    g0: Circle CenterX=-23.5 CenterY=35 CenterZ=0 NormalX=0 NormalY=0 NormalZ=1 AngleXU=0 Radius=2.5
    g1: Circle CenterX=-23.5 CenterY=35 CenterZ=0 NormalX=0 NormalY=0 NormalZ=1 AngleXU=0 Radius=1.3
    g2: Circle CenterX=-23.5 CenterY=13 CenterZ=0 NormalX=0 NormalY=0 NormalZ=1 AngleXU=0 Radius=1.3
    g3: Circle CenterX=-23.5 CenterY=13 CenterZ=0 NormalX=0 NormalY=0 NormalZ=1 AngleXU=0 Radius=2.5
    g4: Circle CenterX=7.5 CenterY=24 CenterZ=0 NormalX=0 NormalY=0 NormalZ=1 AngleXU=0 Radius=3
    g5: Circle CenterX=7.5 CenterY=24 CenterZ=0 NormalX=0 NormalY=0 NormalZ=1 AngleXU=0 Radius=1.3
    g6: LineSegment [constr] StartX=-23.5 StartY=35 StartZ=0 EndX=-23.5 EndY=13 EndZ=0
    g7: LineSegment [constr] StartX=-23.5 StartY=13 StartZ=0 EndX=7.5 EndY=13 EndZ=0
    g8: LineSegment [constr] StartX=7.5 StartY=13 StartZ=0 EndX=7.5 EndY=35 EndZ=0
    g9: LineSegment [constr] StartX=7.5 StartY=35 StartZ=0 EndX=-23.5 EndY=35 EndZ=0
  constraints (25):
    c: Coincident(g1,g0)
    c: Coincident(g3,g2)
    c: Coincident(g5,g4)
    c: Equal(g2,g1)
    c: Equal(g1,g5)
    c: Diameter(g1) = 2.6
    c: Equal(g3,g0)
    c: Diameter(g0) = 5
    c: Diameter(g4) = 6
    c: Coincident(g6,g7)
    c: Coincident(g7,g8)
    c: Coincident(g8,g9)
    c: Coincident(g9,g6)
    c: Vertical(g6)
    c: Vertical(g8)
    c: Horizontal(g7)
    c: Horizontal(g9)
    c: Coincident(g2,g6)
    c: Coincident(g0,g6)
    c: Symmetric(g7,g8,g4)
    c: DistanceY(g2,g0) = 22
    c: DistanceX(g2,g7) = 31
    c: Distance(g2,g-5) = 6
    c: Distance(g-3,g-3) = 48.02
    c: DistanceY(g-4,g2) = 10
FEATURE [PartDesign::Pad] Pad002  label="pcb_standoff"
  BaseFeature = -> Pocket001
  Direction = (0,0,1)
  Length = 4
  Length2 = 10
  Profile = -> Sketch003 [Edge1,Edge5,Edge4]
  ReferenceAxis = -> Sketch003 [N_Axis]
  Refine = true
  Suppressed = false
  Type = 0
FEATURE [PartDesign::Pocket] Pocket002  label="pcb_standoff_pocket"
  BaseFeature = -> Pad002
  Direction = (0,0,-1)
  Length = 5
  Length2 = 5
  Profile = -> Sketch003 [Edge3,Edge2,Edge6]
  ReferenceAxis = -> Sketch003 [N_Axis]
  Refine = true
  Reversed = true
  Suppressed = false
  Type = 1
FEATURE [Sketcher::SketchObject] Sketch004  label="usb_cap"
  ArcFitTolerance = 1e-06
  AttachmentSupport = -> [Pocket002]
  ExternalGeometry = -> [Pocket002]
  ExternalTypes = [0,0]
  FullyConstrained = true
  MakeInternals = false
  MapMode = 5
  Placement = pos=(-32.5,0,0) rot=(0.57735,-0.57735,-0.57735;2.0944rad)
  expr: Constraints[0] = VarSet.Base_usb_cover_main_diameter * 1.2
  expr: Constraints[4] = VarSet.Base_usb_cover_main_diameter
  sketch-geometry (2):
    g0: Circle CenterX=-26 CenterY=-13 CenterZ=0 NormalX=0 NormalY=0 NormalZ=1 AngleXU=0 Radius=10.8
    g1: Circle CenterX=-26 CenterY=-13 CenterZ=0 NormalX=0 NormalY=0 NormalZ=1 AngleXU=0 Radius=9
  constraints (5):
    c: Diameter(g0) = 21.6
    c: Distance(g0,g-2) = 26
    c: DistanceY(g0,g-1) = 13
    c: Coincident(g1,g0)
    c: Diameter(g1) = 18
FEATURE [Sketcher::SketchObject] Sketch005  label="switch_antennas"
  ArcFitTolerance = 1e-06
  ExternalTypes = [0]
  FullyConstrained = true
  MakeInternals = false
  MapMode = 2
  Placement = pos=(0,55,0) rot=(0,0.707107,0.707107;3.14159rad)
  expr: .Placement.Base.y = VarSet.Base_base_lenght
  expr: Constraints[17] = VarSet.base_width
  expr: Constraints[18] = VarSet.case_height
  sketch-geometry (21):
    g0: Circle CenterX=-17 CenterY=-16 CenterZ=0 NormalX=0 NormalY=0 NormalZ=1 AngleXU=0 Radius=3.25
    g1: GeomPoint [constr] X=-17 Y=-16 Z=0
    g2: Circle CenterX=-17 CenterY=-16 CenterZ=0 NormalX=0 NormalY=0 NormalZ=1 AngleXU=0 Radius=7
    g3: Circle CenterX=-17 CenterY=-16 CenterZ=0 NormalX=0 NormalY=0 NormalZ=1 AngleXU=0 Radius=8
    g4: LineSegment [constr] StartX=32.5 StartY=0 StartZ=0 EndX=-32.5 EndY=0 EndZ=0
    g5: LineSegment [constr] StartX=-32.5 StartY=0 StartZ=0 EndX=-32.5 EndY=-25 EndZ=0
    g6: LineSegment [constr] StartX=-32.5 StartY=-25 StartZ=0 EndX=32.5 EndY=-25 EndZ=0
    g7: LineSegment [constr] StartX=32.5 StartY=-25 StartZ=0 EndX=32.5 EndY=0 EndZ=0
    g8: LineSegment StartX=-8.00889 StartY=-18.8 StartZ=0 EndX=5.99111 EndY=-18.8 EndZ=0
    g9: LineSegment StartX=5.99111 StartY=-18.8 StartZ=0 EndX=5.99111 EndY=-16.4 EndZ=0
    g10: LineSegment StartX=5.99111 StartY=-16.4 StartZ=0 EndX=-8.00889 EndY=-16.4 EndZ=0
    g11: LineSegment StartX=-8.00889 StartY=-16.4 StartZ=0 EndX=-8.00889 EndY=-18.8 EndZ=0
    g12: GeomPoint [constr] X=-1.00889 Y=-17.6 Z=0
    g13: LineSegment StartX=-8.00889 StartY=-2.4 StartZ=0 EndX=5.99111 EndY=-2.4 EndZ=0
    g14: LineSegment StartX=5.99111 StartY=-2.4 StartZ=0 EndX=5.99111 EndY=0 EndZ=0
    g15: LineSegment StartX=5.99111 StartY=0 StartZ=0 EndX=-8.00889 EndY=0 EndZ=0
    g16: LineSegment StartX=-8.00889 StartY=0 StartZ=0 EndX=-8.00889 EndY=-2.4 EndZ=0
    g17: GeomPoint [constr] X=-1.00889 Y=-1.2 Z=0
    g18: Circle CenterX=-1.00889 CenterY=-9.4 CenterZ=0 NormalX=0 NormalY=0 NormalZ=1 AngleXU=0 Radius=3
    g19: LineSegment [constr] StartX=-1.00889 StartY=-17.6 StartZ=0 EndX=-1.00889 EndY=-1.2 EndZ=0
    g20: GeomPoint [constr] X=-1.00889 Y=-9.4 Z=0
  constraints (51):
    c: Diameter(g0) = 6.5
    c: Coincident(g0,g1)
    c: Coincident(g2,g0)
    c: Coincident(g3,g0)
    c: Diameter(g2) = 14
    c: Diameter(g3) = 16
    c: DistanceX(g0,g-1) = 17
    c: DistanceY(g0,g-1) = 16
    c: Coincident(g4,g5)
    c: Coincident(g5,g6)
    c: Coincident(g6,g7)
    c: Coincident(g7,g4)
    c: Horizontal(g4)
    c: Vertical(g5)
    c: Vertical(g7)
    c: PointOnObject(g4,g-1)
    c: Symmetric(g5,g6,g-2)
    c: DistanceX(g6,g6) = 65
    c: DistanceY(g6,g-1) = 25
    c: Coincident(g8,g9)
    c: Coincident(g9,g10)
    c: Coincident(g10,g11)
    c: Coincident(g11,g8)
    c: Symmetric(g10,g8,g12)
    c: Coincident(g13,g14)
    c: Coincident(g14,g15)
    c: Coincident(g15,g16)
    c: Coincident(g16,g13)
    c: Symmetric(g15,g13,g17)
    c: Equal(g11,g16)
    c: Equal(g10,g13)
    c: Diameter(g18) = 6
    c: Coincident(g19,g12)
    c: Coincident(g19,g17)
    c: Symmetric(g19,g19,g20)
    c: Coincident(g18,g20)
    c: Distance(g18,g13) = 4
    c: Perpendicular(g9,g8)
    c: Perpendicular(g11,g10)
    c: Perpendicular(g14,g13)
    c: Perpendicular(g16,g15)
    c: Parallel(g10,g13)
    c: Parallel(g8,g15)
    c: Perpendicular(g10,g19)
    c: Perpendicular(g14,g15)
    c: Parallel(g15,g4)
    c: DistanceY(g8,g9) = 2.4
    c: PointOnObject(g15,g4)
    c: DistanceY(g9,g13) = 14
    c: DistanceX(g10,g9) = 14
    c: Distance(g10,g3) = 1
FEATURE [PartDesign::Pocket] Pocket007  label="usb_cap_inside"
  BaseFeature = -> Pocket002
  Direction = (1,0,0)
  Length = 5
  Length2 = 5
  Profile = -> Sketch004 [Edge2]
  ReferenceAxis = -> Sketch004 [N_Axis]
  Refine = true
  Suppressed = false
  Type = 0
FEATURE [PartDesign::Pocket] Pocket008  label="usb_cap_outside"
  BaseFeature = -> Pocket007
  Direction = (1,0,0)
  Length = 1.5
  Length2 = 5
  Profile = -> Sketch004 [Edge1]
  ReferenceAxis = -> Sketch004 [N_Axis]
  Refine = true
  Suppressed = false
  Type = 0
  expr: Length = VarSet.Base_case_thickness / 2
FEATURE [PartDesign::Pocket] Pocket010
  BaseFeature = -> Pocket008
  Direction = (-1e-16,-1,2e-16)
  Length = 3
  Length2 = 5
  Profile = -> Sketch005 [Edge1]
  ReferenceAxis = -> Sketch005 [N_Axis]
  Refine = true
  Suppressed = false
  Type = 0
  expr: Length = VarSet.Base_case_thickness
FEATURE [PartDesign::Pad] Pad007  label="antenna_"
  BaseFeature = -> Pocket010
  Direction = (1e-16,1,-2e-16)
  Length = 10
  Length2 = 10
  Profile = -> Sketch005 [Edge3,Edge2]
  ReferenceAxis = -> Sketch005 [N_Axis]
  Refine = true
  Suppressed = false
  Type = 0
FEATURE [Sketcher::SketchObject] Sketch019  label="pogopins_case002"
  ArcFitTolerance = 1e-06
  AttachmentSupport = -> [XZ_Plane053]
  ExternalTypes = [0]
  FullyConstrained = true
  MakeInternals = false
  MapMode = 5
  Placement = pos=(0,0,0) rot=(1,0,0;1.5708rad)
  expr: Constraints[12] = VarSet.Base_pogopins_r
  expr: Constraints[1] = VarSet.case_height / 2
  expr: Constraints[25] = VarSet.Base_pogoping_lenght
  sketch-geometry (11):
    g0: GeomPoint X=0 Y=-12.5 Z=0
    g1: ArcOfCircle CenterX=-5.45 CenterY=-12.5 CenterZ=0 NormalX=0 NormalY=0 NormalZ=1 AngleXU=0 Radius=2.1 StartAngle=1.5708 EndAngle=4.71239
    g2: ArcOfCircle CenterX=5.45 CenterY=-12.5 CenterZ=0 NormalX=0 NormalY=0 NormalZ=1 AngleXU=0 Radius=2.1 StartAngle=4.71239 EndAngle=7.85398
    g3: LineSegment StartX=-5.45 StartY=-10.4 StartZ=0 EndX=5.45 EndY=-10.4 EndZ=0
    g4: LineSegment StartX=-5.45 StartY=-14.6 StartZ=0 EndX=5.45 EndY=-14.6 EndZ=0
    g5: LineSegment [constr] StartX=-5.45 StartY=-12.5 StartZ=0 EndX=5.45 EndY=-12.5 EndZ=0
    g6: GeomPoint [constr] X=0 Y=-12.5 Z=0
    g7: LineSegment [constr] StartX=-7.55 StartY=-10.4 StartZ=0 EndX=-7.55 EndY=-14.6 EndZ=0
    g8: LineSegment [constr] StartX=-7.55 StartY=-14.6 StartZ=0 EndX=7.55 EndY=-14.6 EndZ=0
    g9: LineSegment [constr] StartX=7.55 StartY=-14.6 StartZ=0 EndX=7.55 EndY=-10.4 EndZ=0
    g10: LineSegment [constr] StartX=7.55 StartY=-10.4 StartZ=0 EndX=-7.55 EndY=-10.4 EndZ=0
  constraints (26):
    c: PointOnObject(g0,g-2)
    c: Distance(g0,g-1) = 12.5
    c: Tangent(g1,g3) = 1.5708
    c: Tangent(g1,g4) = -1.5708
    c: Tangent(g2,g3) = 1.5708
    c: Tangent(g2,g4) = -1.5708
    c: Equal(g1,g2)
    c: Horizontal(g3)
    c: Coincident(g5,g1)
    c: Coincident(g5,g2)
    c: Symmetric(g5,g5,g6)
    c: Coincident(g0,g6)
    c: Radius(g1) = 2.1
    c: Coincident(g7,g8)
    c: Coincident(g8,g9)
    c: Coincident(g9,g10)
    c: Coincident(g10,g7)
    c: Vertical(g7)
    c: Vertical(g9)
    c: Horizontal(g8)
    c: Horizontal(g10)
    c: PointOnObject(g2,g10)
    c: PointOnObject(g2,g8)
    c: Tangent(g2,g9)
    c: Tangent(g7,g1)
    c: DistanceX(g7,g9) = 15.1
FEATURE [Sketcher::SketchObject] Sketch020  label="pogoPins_outside"
  ArcFitTolerance = 1e-06
  ExternalTypes = [0]
  FullyConstrained = true
  MakeInternals = false
  MapMode = 5
  Placement = pos=(0,3,0) rot=(0,0.707107,0.707107;3.14159rad)
  expr: Constraints[11] = VarSet.case_height / 2
  expr: Constraints[12] = VarSet.Base_pogopin_outside
  expr: Constraints[13] = 3 * VarSet.Base_pogopins_r
  sketch-geometry (6):
    g0: GeomPoint [constr] X=0 Y=-12.5 Z=0
    g1: LineSegment StartX=-10.5 StartY=-15.65 StartZ=0 EndX=-10.5 EndY=-9.35 EndZ=0
    g2: LineSegment StartX=-10.5 StartY=-9.35 StartZ=0 EndX=10.5 EndY=-9.35 EndZ=0
    g3: LineSegment StartX=10.5 StartY=-9.35 StartZ=0 EndX=10.5 EndY=-15.65 EndZ=0
    g4: LineSegment StartX=10.5 StartY=-15.65 StartZ=0 EndX=-10.5 EndY=-15.65 EndZ=0
    g5: GeomPoint [constr] X=0 Y=-12.5 Z=0
  constraints (14):
    c: PointOnObject(g0,g-2)
    c: Coincident(g1,g2)
    c: Coincident(g2,g3)
    c: Coincident(g3,g4)
    c: Coincident(g4,g1)
    c: Vertical(g1)
    c: Vertical(g3)
    c: Horizontal(g2)
    c: Horizontal(g4)
    c: Symmetric(g3,g1,g5)
    c: Coincident(g5,g0)
    c: DistanceY(g0,g-1) = 12.5
    c: DistanceX(g1,g2) = 21
    c: DistanceY(g3,g2) = 6.3
FEATURE [PartDesign::Pocket] Pocket018  label="pogoPins_outside001"
  BaseFeature = -> Pad007
  Direction = (-1e-16,-1,2e-16)
  Length = 3
  Length2 = 5
  Profile = -> Sketch020
  ReferenceAxis = -> Sketch020 [N_Axis]
  Refine = true
  Suppressed = false
  Type = 0
  expr: Length = VarSet.Base_case_thickness
FEATURE [Sketcher::SketchObject] Sketch024  label="nuts"
  ArcFitTolerance = 1e-06
  AttachmentSupport = -> [Pocket018]
  ExternalGeometry = -> [Pocket018]
  ExternalTypes = [0,0,0,0]
  FullyConstrained = true
  MakeInternals = false
  MapMode = 5
  Placement = pos=(0,0,-25) rot=(1,0,0;3.14159rad)
  sketch-geometry (28):
    g0: LineSegment StartX=-27.0566 StartY=-6.5 StartZ=0 EndX=-25.6132 EndY=-4 EndZ=0
    g1: LineSegment StartX=-25.6132 StartY=-4 StartZ=0 EndX=-27.0566 EndY=-1.5 EndZ=0
    g2: LineSegment StartX=-27.0566 StartY=-1.5 StartZ=0 EndX=-29.9434 EndY=-1.5 EndZ=0
    g3: LineSegment StartX=-29.9434 StartY=-1.5 StartZ=0 EndX=-31.3868 EndY=-4 EndZ=0
    g4: LineSegment StartX=-31.3868 StartY=-4 StartZ=0 EndX=-29.9434 EndY=-6.5 EndZ=0
    g5: LineSegment StartX=-29.9434 StartY=-6.5 StartZ=0 EndX=-27.0566 EndY=-6.5 EndZ=0
    g6: Circle [constr] CenterX=-28.5 CenterY=-4 CenterZ=0 NormalX=0 NormalY=0 NormalZ=1 AngleXU=0 Radius=2.88675
    g7: LineSegment StartX=25.6132 StartY=-4 StartZ=0 EndX=27.0566 EndY=-6.5 EndZ=0
    g8: LineSegment StartX=27.0566 StartY=-6.5 StartZ=0 EndX=29.9434 EndY=-6.5 EndZ=0
    g9: LineSegment StartX=29.9434 StartY=-6.5 StartZ=0 EndX=31.3868 EndY=-4 EndZ=0
    g10: LineSegment StartX=31.3868 StartY=-4 StartZ=0 EndX=29.9434 EndY=-1.5 EndZ=0
    g11: LineSegment StartX=29.9434 StartY=-1.5 StartZ=0 EndX=27.0566 EndY=-1.5 EndZ=0
    g12: LineSegment StartX=27.0566 StartY=-1.5 StartZ=0 EndX=25.6132 EndY=-4 EndZ=0
    g13: Circle [constr] CenterX=28.5 CenterY=-4 CenterZ=0 NormalX=0 NormalY=0 NormalZ=1 AngleXU=0 Radius=2.88675
    g14: LineSegment StartX=27.0566 StartY=-48.5 StartZ=0 EndX=25.6132 EndY=-51 EndZ=0
    g15: LineSegment StartX=25.6132 StartY=-51 StartZ=0 EndX=27.0566 EndY=-53.5 EndZ=0
    g16: LineSegment StartX=27.0566 StartY=-53.5 StartZ=0 EndX=29.9434 EndY=-53.5 EndZ=0
    g17: LineSegment StartX=29.9434 StartY=-53.5 StartZ=0 EndX=31.3868 EndY=-51 EndZ=0
    g18: LineSegment StartX=31.3868 StartY=-51 StartZ=0 EndX=29.9434 EndY=-48.5 EndZ=0
    g19: LineSegment StartX=29.9434 StartY=-48.5 StartZ=0 EndX=27.0566 EndY=-48.5 EndZ=0
    g20: Circle [constr] CenterX=28.5 CenterY=-51 CenterZ=0 NormalX=0 NormalY=0 NormalZ=1 AngleXU=0 Radius=2.88675
    g21: LineSegment StartX=-25.6132 StartY=-51 StartZ=0 EndX=-27.0566 EndY=-48.5 EndZ=0
    g22: LineSegment StartX=-27.0566 StartY=-48.5 StartZ=0 EndX=-29.9434 EndY=-48.5 EndZ=0
    g23: LineSegment StartX=-29.9434 StartY=-48.5 StartZ=0 EndX=-31.3868 EndY=-51 EndZ=0
    g24: LineSegment StartX=-31.3868 StartY=-51 StartZ=0 EndX=-29.9434 EndY=-53.5 EndZ=0
    g25: LineSegment StartX=-29.9434 StartY=-53.5 StartZ=0 EndX=-27.0566 EndY=-53.5 EndZ=0
    g26: LineSegment StartX=-27.0566 StartY=-53.5 StartZ=0 EndX=-25.6132 EndY=-51 EndZ=0
    g27: Circle [constr] CenterX=-28.5 CenterY=-51 CenterZ=0 NormalX=0 NormalY=0 NormalZ=1 AngleXU=0 Radius=2.88675
  constraints (64):
    c: Coincident(g0,g1)
    c: Coincident(g1,g2)
    c: Coincident(g2,g3)
    c: Coincident(g3,g4)
    c: Coincident(g4,g5)
    c: Coincident(g5,g0)
    c: Equal(g0, g1-g5) x5
    c: PointOnObject(g0,g6)
    c: PointOnObject(g1,g6)
    c: PointOnObject(g2,g6)
    c: PointOnObject(g3,g6)
    c: PointOnObject(g4,g6)
    c: PointOnObject(g5,g6)
    c: Coincident(g6,g-3)
    c: Coincident(g7,g8)
    c: Coincident(g8,g9)
    c: Coincident(g9,g10)
    c: Coincident(g10,g11)
    c: Coincident(g11,g12)
    c: Coincident(g12,g7)
    c: Equal(g7, g8-g12) x5
    c: PointOnObject(g7,g13)
    c: PointOnObject(g8,g13)
    c: PointOnObject(g9,g13)
    c: PointOnObject(g10,g13)
    c: PointOnObject(g11,g13)
    c: PointOnObject(g12,g13)
    c: Coincident(g13,g-4)
    c: Coincident(g14,g15)
    c: Coincident(g15,g16)
    c: Coincident(g16,g17)
    c: Coincident(g17,g18)
    c: Coincident(g18,g19)
    c: Coincident(g19,g14)
    c: Equal(g14, g15-g19) x5
    c: PointOnObject(g14,g20)
    c: PointOnObject(g15,g20)
    c: PointOnObject(g16,g20)
    c: PointOnObject(g17,g20)
    c: PointOnObject(g18,g20)
    c: PointOnObject(g19,g20)
    c: Coincident(g20,g-5)
    c: Coincident(g21,g22)
    c: Coincident(g22,g23)
    c: Coincident(g23,g24)
    c: Coincident(g24,g25)
    c: Coincident(g25,g26)
    c: Coincident(g26,g21)
    c: Equal(g21, g22-g26) x5
    c: PointOnObject(g21,g27)
    c: PointOnObject(g22,g27)
    c: PointOnObject(g23,g27)
    c: PointOnObject(g24,g27)
    c: PointOnObject(g25,g27)
    c: PointOnObject(g26,g27)
    c: Coincident(g27,g-6)
    c: Parallel(g22,g-1)
    c: Parallel(g2,g-1)
    c: Parallel(g-1,g11)
    c: Parallel(g19,g-1)
    c: Equal(g27,g20)
    c: Equal(g20,g13)
    c: Equal(g13,g6)
    c: Distance(g2,g5) = 5
FEATURE [PartDesign::Pocket] Pocket025  label="nuts002"
  BaseFeature = -> Pocket018
  Direction = (0,0,1)
  Length = 20
  Length2 = 5
  Profile = -> Sketch024
  ReferenceAxis = -> Sketch024 [N_Axis]
  Refine = true
  Suppressed = false
  Type = 0
  expr: Length = VarSet.case_height * 0.8
FEATURE [Sketcher::SketchObject] Sketch032  label="gasket001"
  ArcFitTolerance = 1e-06
  AttachmentSupport = -> [YZ_Plane053]
  ExternalGeometry = -> [Sketch]
  ExternalTypes = [0]
  FullyConstrained = true
  MakeInternals = false
  MapMode = 5
  Placement = pos=(0,0,0) rot=(0.57735,0.57735,0.57735;2.0944rad)
  expr: Constraints[10] = VarSet.Base_gasket_width
  expr: Constraints[11] = VarSet.Base_gasket_height
  sketch-geometry (5):
    g0: LineSegment StartX=1 StartY=1 StartZ=0 EndX=1 EndY=-1 EndZ=0
    g1: LineSegment StartX=1 StartY=-1 StartZ=0 EndX=2 EndY=-1 EndZ=0
    g2: LineSegment StartX=2 StartY=-1 StartZ=0 EndX=2 EndY=1 EndZ=0
    g3: LineSegment StartX=2 StartY=1 StartZ=0 EndX=1 EndY=1 EndZ=0
    g4: GeomPoint [constr] X=1.5 Y=0 Z=0
  constraints (12):
    c: Coincident(g0,g1)
    c: Coincident(g1,g2)
    c: Coincident(g2,g3)
    c: Coincident(g3,g0)
    c: Vertical(g0)
    c: Vertical(g2)
    c: Horizontal(g1)
    c: Horizontal(g3)
    c: Symmetric(g2,g0,g4)
    c: Coincident(g4,g-3)
    c: DistanceX(g0,g2) = 1
    c: DistanceY(g0,g0) = 2
FEATURE [PartDesign::SubtractivePipe] SubtractivePipe
  AuxilleryCurvelinear = true
  AuxillerySpineTangent = false
  BaseFeature = -> Pocket025
  Binormal = (0,0,0)
  Mode = 0
  Profile = -> Sketch032
  Refine = true
  Spine = -> Sketch [Edge21,Edge20,Edge19,Edge34,Edge33,Edge32,Edge31,Edge30,Edge29,Edge28,Edge27,Edge26,Edge25,Edge24,Edge23,Edge22]
  SpineTangent = false
  Suppressed = false
  Transformation = 0
  Transition = 0
FEATURE [PartDesign::Pocket] Pocket028  label="onoff_"
  BaseFeature = -> SubtractivePipe
  Direction = (-1e-16,-1,2e-16)
  Length = 3
  Length2 = 5
  Profile = -> Sketch005 [Edge12]
  ReferenceAxis = -> Sketch005 [N_Axis]
  Refine = true
  Suppressed = false
  Type = 0
  expr: Length = VarSet.Base_case_thickness
FEATURE [PartDesign::Pad] Pad020
  BaseFeature = -> Pocket028
  Direction = (1e-16,1,-2e-16)
  Length = 20
  Length2 = 10
  Profile = -> Sketch005 [Edge10,Edge9,Edge8,Edge11,Edge6,Edge7,Edge4,Edge5]
  ReferenceAxis = -> Sketch005 [N_Axis]
  Refine = true
  Suppressed = false
  Type = 0
FEATURE [Sketcher::SketchObject] Sketch046  label="gps_mount"
  ArcFitTolerance = 1e-06
  AttachmentOffset = pos=(0,0,-5) rot=(0,0,1;0rad)
  AttachmentSupport = -> [XY_Plane053]
  ExternalTypes = [0]
  FullyConstrained = true
  MakeInternals = false
  MapMode = 5
  Placement = pos=(0,0,-5) rot=(0,0,1;0rad)
  expr: Constraints[10] = 50 mm
  expr: Constraints[8] = VarSet.Base_base_lenght - VarSet.Base_case_thickness
  sketch-geometry (16):
    g0: LineSegment [constr] StartX=-25 StartY=0 StartZ=0 EndX=25 EndY=0 EndZ=0
    g1: LineSegment [constr] StartX=25 StartY=0 StartZ=0 EndX=25 EndY=52 EndZ=0
    g2: LineSegment [constr] StartX=25 StartY=52 StartZ=0 EndX=-25 EndY=52 EndZ=0
    g3: LineSegment [constr] StartX=-25 StartY=52 StartZ=0 EndX=-25 EndY=0 EndZ=0
    g4: LineSegment StartX=-25 StartY=52 StartZ=0 EndX=-25 EndY=44.8 EndZ=0
    g5: LineSegment StartX=-23.5 StartY=46 StartZ=0 EndX=-23.5 EndY=52 EndZ=0
    g6: LineSegment StartX=-23.5 StartY=52 StartZ=0 EndX=-25 EndY=52 EndZ=0
    g7: LineSegment StartX=-23.5 StartY=46 StartZ=0 EndX=-22.5 EndY=46 EndZ=0
    g8: LineSegment StartX=-22.5 StartY=46 StartZ=0 EndX=-22.5 EndY=44.8 EndZ=0
    g9: LineSegment StartX=-22.5 StartY=44.8 StartZ=0 EndX=-25 EndY=44.8 EndZ=0
    g10: LineSegment StartX=-6.9 StartY=52 StartZ=0 EndX=-8.4 EndY=52 EndZ=0
    g11: LineSegment StartX=-6.9 StartY=44.8 StartZ=0 EndX=-9.4 EndY=44.8 EndZ=0
    g12: LineSegment StartX=-9.4 StartY=46 StartZ=0 EndX=-8.4 EndY=46 EndZ=0
    g13: LineSegment StartX=-8.4 StartY=46 StartZ=0 EndX=-8.4 EndY=52 EndZ=0
    g14: LineSegment StartX=-6.9 StartY=52 StartZ=0 EndX=-6.9 EndY=44.8 EndZ=0
    g15: LineSegment StartX=-9.4 StartY=44.8 StartZ=0 EndX=-9.4 EndY=46 EndZ=0
  constraints (46):
    c: Coincident(g0,g1)
    c: Coincident(g1,g2)
    c: Coincident(g2,g3)
    c: Coincident(g3,g0)
    c: Horizontal(g0)
    c: Vertical(g1)
    c: Vertical(g3)
    c: PointOnObject(g0,g-1)
    c: DistanceY(g0,g2) = 52
    c: Symmetric(g2,g1,g-2)
    c: DistanceX(g2,g1) = 50
    c: Coincident(g2,g4)
    c: PointOnObject(g4,g3)
    c: PointOnObject(g5,g2)
    c: Vertical(g5)
    c: Coincident(g5,g6)
    c: Coincident(g6,g4)
    c: Distance(g2,g5) = 1.5
    c: Coincident(g5,g7)
    c: Horizontal(g7)
    c: Coincident(g7,g8)
    c: Vertical(g8)
    c: Coincident(g9,g8)
    c: Coincident(g9,g4)
    c: Horizontal(g9)
    c: Distance(g5,g7) = 1
    c: Distance(g5,g6) = 6
    c: DistanceY(g8,g7) = 1.2
    c: PointOnObject(g10,g2)
    c: PointOnObject(g10,g2)
    c: Equal(g6,g10)
    c: Horizontal(g11)
    c: Coincident(g12,g13)
    c: Coincident(g13,g10)
    c: Perpendicular(g13,g12)
    c: Equal(g9,g11)
    c: Equal(g7,g12)
    c: Equal(g5,g13)
    c: DistanceX(g5,g12) = 15.1
    c: Coincident(g14,g10)
    c: Coincident(g14,g11)
    c: Vertical(g14)
    c: Coincident(g15,g11)
    c: Coincident(g15,g12)
    c: Vertical(g15)
    c: Equal(g8,g15)
FEATURE [PartDesign::Pad] Pad021  label="gps_mount001"
  BaseFeature = -> Pad020
  Direction = (0,0,1)
  Length = 18
  Length2 = 10
  Profile = -> Sketch046
  ReferenceAxis = -> Sketch046 [N_Axis]
  Refine = true
  Reversed = true
  Suppressed = false
  Type = 0
FEATURE [Sketcher::SketchObject] Sketch047  label="on_off_sma"
  ArcFitTolerance = 1e-06
  AttachmentSupport = -> [Pad021]
  ExternalGeometry = -> [Pad021]
  ExternalTypes = [0,0]
  FullyConstrained = true
  MakeInternals = false
  MapMode = 5
  Placement = pos=(0,52,0) rot=(1,0,0;1.5708rad)
  expr: Constraints[10] = 13.2
  sketch-geometry (12):
    g0: LineSegment StartX=-5.59111 StartY=-5.25 StartZ=0 EndX=-5.59111 EndY=-13.55 EndZ=0
    g1: LineSegment StartX=-5.59111 StartY=-13.55 StartZ=0 EndX=7.60889 EndY=-13.55 EndZ=0
    g2: LineSegment StartX=7.60889 StartY=-13.55 StartZ=0 EndX=7.60889 EndY=-5.25 EndZ=0
    g3: LineSegment StartX=7.60889 StartY=-5.25 StartZ=0 EndX=-5.59111 EndY=-5.25 EndZ=0
    g4: GeomPoint [constr] X=1.00889 Y=-9.4 Z=0
    g5: LineSegment StartX=19.3671 StartY=-20.1 StartZ=0 EndX=21.7343 EndY=-16 EndZ=0
    g6: LineSegment StartX=21.7343 StartY=-16 StartZ=0 EndX=19.3671 EndY=-11.9 EndZ=0
    g7: LineSegment StartX=19.3671 StartY=-11.9 StartZ=0 EndX=14.6329 EndY=-11.9 EndZ=0
    g8: LineSegment StartX=14.6329 StartY=-11.9 StartZ=0 EndX=12.2657 EndY=-16 EndZ=0
    g9: LineSegment StartX=12.2657 StartY=-16 StartZ=0 EndX=14.6329 EndY=-20.1 EndZ=0
    g10: LineSegment StartX=14.6329 StartY=-20.1 StartZ=0 EndX=19.3671 EndY=-20.1 EndZ=0
    g11: Circle [constr] CenterX=17 CenterY=-16 CenterZ=0 NormalX=0 NormalY=0 NormalZ=1 AngleXU=0 Radius=4.73427
  constraints (28):
    c: Coincident(g0,g1)
    c: Coincident(g1,g2)
    c: Coincident(g2,g3)
    c: Coincident(g3,g0)
    c: Vertical(g0)
    c: Vertical(g2)
    c: Horizontal(g1)
    c: Horizontal(g3)
    c: Symmetric(g2,g0,g4)
    c: Coincident(g4,g-3)
    c: DistanceX(g0,g2) = 13.2
    c: DistanceY(g0,g0) = 8.3
    c: Coincident(g5,g6)
    c: Coincident(g6,g7)
    c: Coincident(g7,g8)
    c: Coincident(g8,g9)
    c: Coincident(g9,g10)
    c: Coincident(g10,g5)
    c: Equal(g5, g6-g10) x5
    c: PointOnObject(g5,g11)
    c: PointOnObject(g6,g11)
    c: PointOnObject(g7,g11)
    c: PointOnObject(g8,g11)
    c: PointOnObject(g9,g11)
    c: PointOnObject(g10,g11)
    c: Coincident(g11,g-4)
    c: Parallel(g7,g-1)
    c: DistanceY(g9,g7) = 8.2
FEATURE [PartDesign::Pocket] Pocket029  label="onff_sma_recess"
  BaseFeature = -> Pad021
  Direction = (0,1,-2e-16)
  Length = 0.6
  Length2 = 5
  Profile = -> Sketch047
  ReferenceAxis = -> Sketch047 [N_Axis]
  Refine = true
  Suppressed = false
  Type = 0
  expr: Length = VarSet.Base_case_thickness * 0.2
FEATURE [Sketcher::SketchObject] Sketch051  label="clips_outside"
  ArcFitTolerance = 1e-06
  ExternalTypes = [0,0]
  FullyConstrained = true
  MakeInternals = false
  MapMode = 5
  Placement = pos=(0,-12,0) rot=(1,0,0;1.5708rad)
  expr: Constraints[23] = VarSet.Base_connector_clip
  sketch-geometry (13):
    g0: GeomPoint X=-32.5 Y=-12.5 Z=0
    g1: GeomPoint X=32.5 Y=-12.5 Z=0
    g2: LineSegment [constr] StartX=-32.5 StartY=-12.5 StartZ=0 EndX=32.5 EndY=-12.5 EndZ=0
    g3: LineSegment StartX=-31.5 StartY=-8.5 StartZ=0 EndX=-31.5 EndY=-16.5 EndZ=0
    g4: LineSegment StartX=-31.5 StartY=-16.5 StartZ=0 EndX=-23.5 EndY=-16.5 EndZ=0
    g5: LineSegment StartX=-23.5 StartY=-16.5 StartZ=0 EndX=-23.5 EndY=-8.5 EndZ=0
    g6: LineSegment StartX=-23.5 StartY=-8.5 StartZ=0 EndX=-31.5 EndY=-8.5 EndZ=0
    g7: GeomPoint [constr] X=-27.5 Y=-12.5 Z=0
    g8: LineSegment StartX=23.5 StartY=-8.5 StartZ=0 EndX=23.5 EndY=-16.5 EndZ=0
    g9: LineSegment StartX=23.5 StartY=-16.5 StartZ=0 EndX=31.5 EndY=-16.5 EndZ=0
    g10: LineSegment StartX=31.5 StartY=-16.5 StartZ=0 EndX=31.5 EndY=-8.5 EndZ=0
    g11: LineSegment StartX=31.5 StartY=-8.5 StartZ=0 EndX=23.5 EndY=-8.5 EndZ=0
    g12: GeomPoint [constr] X=27.5 Y=-12.5 Z=0
  constraints (29):
    c: Symmetric(g-3,g-3,g0)
    c: Symmetric(g-4,g-4,g1)
    c: Coincident(g2,g0)
    c: Coincident(g2,g1)
    c: Coincident(g3,g4)
    c: Coincident(g4,g5)
    c: Coincident(g5,g6)
    c: Coincident(g6,g3)
    c: Vertical(g3)
    c: Vertical(g5)
    c: Horizontal(g4)
    c: Horizontal(g6)
    c: Symmetric(g5,g3,g7)
    c: PointOnObject(g7,g2)
    c: Coincident(g8,g9)
    c: Coincident(g9,g10)
    c: Coincident(g10,g11)
    c: Coincident(g11,g8)
    c: Vertical(g8)
    c: Vertical(g10)
    c: Horizontal(g9)
    c: Horizontal(g11)
    c: Symmetric(g10,g8,g12)
    c: DistanceX(g3,g5) = 8
    c: Equal(g6,g3)
    c: Equal(g3,g8)
    c: Equal(g8,g11)
    c: Symmetric(g7,g12,g-2)
    c: DistanceX(g0,g7) = 5
FEATURE [Sketcher::SketchObject] Sketch052  label="clips_inside"
  ArcFitTolerance = 1e-06
  AttachmentOffset = pos=(0,0,-1.6) rot=(0,0,1;0rad)
  ExternalGeometry = -> [Sketch051]
  ExternalTypes = [0,0,0,0]
  FullyConstrained = true
  MakeInternals = false
  MapMode = 5
  Placement = pos=(0,-10.4,0) rot=(1,0,0;1.5708rad)
  expr: .AttachmentOffset.Base.z = -1 * VarSet.Base_connector_clip_height
  expr: .Placement.Base.y = -1 * (VarSet.Base_connector_height_lug - VarSet.Base_connector_clip_height)
  expr: Constraints[26] = VarSet.Base_connector_clip * 0.5
  sketch-geometry (14):
    g0: LineSegment [constr] StartX=-31.5 StartY=-16.5 StartZ=0 EndX=-23.5 EndY=-8.5 EndZ=0
    g1: LineSegment [constr] StartX=23.5 StartY=-16.5 StartZ=0 EndX=31.5 EndY=-8.5 EndZ=0
    g2: GeomPoint [constr] X=-27.5 Y=-12.5 Z=0
    g3: GeomPoint [constr] X=27.5 Y=-12.5 Z=0
    g4: LineSegment StartX=-29.5 StartY=-10.5 StartZ=0 EndX=-29.5 EndY=-14.5 EndZ=0
    g5: LineSegment StartX=-29.5 StartY=-14.5 StartZ=0 EndX=-25.5 EndY=-14.5 EndZ=0
    g6: LineSegment StartX=-25.5 StartY=-14.5 StartZ=0 EndX=-25.5 EndY=-10.5 EndZ=0
    g7: LineSegment StartX=-25.5 StartY=-10.5 StartZ=0 EndX=-29.5 EndY=-10.5 EndZ=0
    g8: GeomPoint [constr] X=-27.5 Y=-12.5 Z=0
    g9: LineSegment StartX=25.5 StartY=-10.5 StartZ=0 EndX=25.5 EndY=-14.5 EndZ=0
    g10: LineSegment StartX=25.5 StartY=-14.5 StartZ=0 EndX=29.5 EndY=-14.5 EndZ=0
    g11: LineSegment StartX=29.5 StartY=-14.5 StartZ=0 EndX=29.5 EndY=-10.5 EndZ=0
    g12: LineSegment StartX=29.5 StartY=-10.5 StartZ=0 EndX=25.5 EndY=-10.5 EndZ=0
    g13: GeomPoint [constr] X=27.5 Y=-12.5 Z=0
  constraints (30):
    c: Coincident(g0,g-3)
    c: Coincident(g0,g-4)
    c: Coincident(g1,g-5)
    c: Coincident(g1,g-6)
    c: Symmetric(g0,g0,g2)
    c: Symmetric(g1,g1,g3)
    c: Coincident(g4,g5)
    c: Coincident(g5,g6)
    c: Coincident(g6,g7)
    c: Coincident(g7,g4)
    c: Vertical(g4)
    c: Vertical(g6)
    c: Horizontal(g5)
    c: Horizontal(g7)
    c: Symmetric(g6,g4,g8)
    c: Coincident(g8,g2)
    c: Coincident(g9,g10)
    c: Coincident(g10,g11)
    c: Coincident(g11,g12)
    c: Coincident(g12,g9)
    c: Vertical(g9)
    c: Vertical(g11)
    c: Horizontal(g10)
    c: Horizontal(g12)
    c: Symmetric(g11,g9,g13)
    c: Coincident(g13,g3)
    c: DistanceX(g4,g6) = 4
    c: Equal(g7,g4)
    c: Equal(g4,g12)
    c: Equal(g12,g11)
FEATURE [PartDesign::SubtractiveLoft] SubtractiveLoft  label="clips_battery"
  BaseFeature = -> Fillet
  Closed = false
  Placement = pos=(0,0,0) rot=(1,0,0;1.5708rad)
  Profile = -> Sketch051
  Refine = true
  Ruled = false
  Sections = -> [Sketch052]
  Suppressed = false
FEATURE [Sketcher::SketchObject] Sketch056  label="cross_section"
  ArcFitTolerance = 1e-06
  AttacherType = Attacher::AttachEngine3D
  AttachmentSupport = -> [SubtractiveLoft]
  ExternalTypes = [0]
  FullyConstrained = true
  MakeInternals = false
  MapMode = 5
  Placement = pos=(0,-12,0) rot=(1,0,0;1.5708rad)
  expr: Constraints[1] = VarSet.case_height / 2
  expr: Constraints[3] = VarSet.Base_connector_oring_outside_diameter - VarSet.Base_connector_oring_cross_section
  sketch-geometry (2):
    g0: GeomPoint X=0 Y=-12.5 Z=0
    g1: Circle CenterX=0 CenterY=-12.5 CenterZ=0 NormalX=0 NormalY=0 NormalZ=1 AngleXU=0 Radius=9.5
  constraints (4):
    c: PointOnObject(g0,g-2)
    c: DistanceY(g0,g-1) = 12.5
    c: Coincident(g1,g0)
    c: Diameter(g1) = 19
FEATURE [Sketcher::SketchObject] Sketch058  label="_oring_diameter"
  ArcFitTolerance = 1e-06
  AttachmentSupport = -> [YZ_Plane066]
  ExternalGeometry = -> [Sketch056]
  ExternalTypes = [0]
  FullyConstrained = false
  MakeInternals = false
  MapMode = 5
  Placement = pos=(0,0,0) rot=(0.57735,0.57735,0.57735;2.0944rad)
  expr: Constraints[0] = VarSet.Base_connector_oring_cross_section
  expr: Constraints[4] = VarSet.Base_connector_oring_offset
  sketch-geometry (2):
    g0: Circle CenterX=-12.2 CenterY=-3 CenterZ=0 NormalX=0 NormalY=0 NormalZ=1 AngleXU=0 Radius=1
    g1: LineSegment [constr] StartX=-16.3675 StartY=-3 StartZ=0 EndX=-7.63249 EndY=-3 EndZ=0
  constraints (5):
    c: Diameter(g0) = 2
    c: PointOnObject(g-3,g1)
    c: PointOnObject(g0,g1)
    c: Symmetric(g1,g1,g-3)
    c: Distance(g0,g-3) = 0.2
FEATURE [PartDesign::SubtractivePipe] SubtractivePipe006
  AuxilleryCurvelinear = true
  AuxillerySpineTangent = false
  BaseFeature = -> SubtractiveLoft
  Binormal = (0,0,0)
  Mode = 0
  Placement = pos=(0,0,0) rot=(1,0,0;1.5708rad)
  Profile = -> Sketch058
  Refine = true
  Spine = -> Sketch056 [Edge1]
  SpineTangent = false
  Suppressed = false
  Transformation = 0
  Transition = 0
FEATURE [PartDesign::Fillet] Fillet003
  Base = -> SubtractivePipe006 [Edge62,Edge49,Edge87,Edge45,Edge56,Edge53,Edge64,Edge51]
  BaseFeature = -> SubtractivePipe006
  Placement = pos=(0,0,0) rot=(1,0,0;1.5708rad)
  Radius = 1
  Refine = true
  SupportTransform = false
  Suppressed = false
  UseAllEdges = false
FEATURE [PartDesign::Body] Body006  label="main_connector001"
  AllowCompound = false
  Group = -> [Sketch013,Sketch014,Sketch016,Sketch017,Pad010,Pocket021,Pocket022,Pocket023,Sketch023,Pocket024,Fillet,Sketch051,Sketch052,SubtractiveLoft,Sketch056,Sketch058,SubtractivePipe006,Fillet003]
  Origin = -> Origin133
  Placement = pos=(3.1e-15,0,-25) rot=(0,1,0;3.14159rad)
  Tip = -> Fillet003
FEATURE [Sketcher::SketchObject] Sketch063  label="strap"
  ArcFitTolerance = 1e-06
  AttachmentOffset = pos=(0,0,-25) rot=(0,0,1;0rad)
  AttachmentSupport = -> [XY_Plane053]
  ExternalTypes = [0]
  FullyConstrained = true
  MakeInternals = false
  MapMode = 5
  Placement = pos=(0,0,-25) rot=(0,0,1;0rad)
  expr: .AttachmentOffset.Base.z = -1 * VarSet.case_height
  expr: Constraints[10] = VarSet.Base_base_lenght
  expr: Constraints[9] = VarSet.base_width
  sketch-geometry (20):
    g0: LineSegment [constr] StartX=-32.5 StartY=0 StartZ=0 EndX=32.5 EndY=0 EndZ=0
    g1: LineSegment [constr] StartX=32.5 StartY=0 StartZ=0 EndX=32.5 EndY=55 EndZ=0
    g2: LineSegment [constr] StartX=32.5 StartY=55 StartZ=0 EndX=-32.5 EndY=55 EndZ=0
    g3: LineSegment [constr] StartX=-32.5 StartY=55 StartZ=0 EndX=-32.5 EndY=0 EndZ=0
    g4: LineSegment StartX=-7 StartY=55 StartZ=0 EndX=-7 EndY=59 EndZ=0
    g5: LineSegment StartX=-10 StartY=62 StartZ=0 EndX=-23 EndY=62 EndZ=0
    g6: LineSegment StartX=-26 StartY=59 StartZ=0 EndX=-26 EndY=55 EndZ=0
    g7: LineSegment StartX=-9 StartY=55 StartZ=0 EndX=-9 EndY=57 EndZ=0
    g8: LineSegment StartX=-12 StartY=60 StartZ=0 EndX=-21 EndY=60 EndZ=0
    g9: LineSegment StartX=-24 StartY=57 StartZ=0 EndX=-24 EndY=55 EndZ=0
    g10: ArcOfCircle CenterX=-23 CenterY=59 CenterZ=0 NormalX=0 NormalY=0 NormalZ=1 AngleXU=0 Radius=3 StartAngle=1.5708 EndAngle=3.14159
    g11: GeomPoint [constr] X=-26 Y=62 Z=0
    g12: ArcOfCircle CenterX=-21 CenterY=57 CenterZ=0 NormalX=0 NormalY=0 NormalZ=1 AngleXU=0 Radius=3 StartAngle=1.5708 EndAngle=3.14159
    g13: GeomPoint [constr] X=-24 Y=60 Z=0
    g14: ArcOfCircle CenterX=-12 CenterY=57 CenterZ=0 NormalX=0 NormalY=0 NormalZ=1 AngleXU=0 Radius=3 StartAngle=2e-16 EndAngle=1.5708
    g15: GeomPoint [constr] X=-9 Y=60 Z=0
    g16: ArcOfCircle CenterX=-10 CenterY=59 CenterZ=0 NormalX=0 NormalY=0 NormalZ=1 AngleXU=0 Radius=3 StartAngle=-9e-16 EndAngle=1.5708
    g17: GeomPoint [constr] X=-7 Y=62 Z=0
    g18: LineSegment StartX=-26 StartY=55 StartZ=0 EndX=-24 EndY=55 EndZ=0
    g19: LineSegment StartX=-9 StartY=55 StartZ=0 EndX=-7 EndY=55 EndZ=0
  constraints (51):
    c: Coincident(g0,g1)
    c: Coincident(g1,g2)
    c: Coincident(g2,g3)
    c: Coincident(g3,g0)
    c: Horizontal(g0)
    c: Vertical(g1)
    c: Vertical(g3)
    c: PointOnObject(g0,g-1)
    c: Symmetric(g2,g1,g-2)
    c: DistanceX(g2,g1) = 65
    c: DistanceY(g-1,g1) = 55
    c: Horizontal(g5)
    c: Vertical(g4)
    c: Vertical(g6)
    c: PointOnObject(g6,g2)
    c: Horizontal(g8)
    c: Vertical(g7)
    c: Vertical(g9)
    c: PointOnObject(g11,g6)
    c: PointOnObject(g11,g5)
    c: Tangent(g6,g10) = -1.5708
    c: Tangent(g5,g10) = -1.5708
    c: PointOnObject(g13,g9)
    c: PointOnObject(g13,g8)
    c: Tangent(g9,g12) = -1.5708
    c: Tangent(g8,g12) = -1.5708
    c: PointOnObject(g15,g7)
    c: PointOnObject(g15,g8)
    c: Tangent(g7,g14) = -1.5708
    c: Tangent(g8,g14) = -1.5708
    c: PointOnObject(g17,g5)
    c: PointOnObject(g17,g4)
    c: Tangent(g5,g16) = -1.5708
    c: Tangent(g4,g16) = -1.5708
    c: Equal(g10,g16)
    c: Equal(g12,g14)
    c: Distance(g6,g9) = 2
    c: Coincident(g18,g6)
    c: Coincident(g18,g9)
    c: Horizontal(g18)
    c: Coincident(g19,g7)
    c: Coincident(g19,g4)
    c: Horizontal(g19)
    c: Equal(g18,g19)
    c: Radius(g10) = 3
    c: Equal(g10,g12)
    c: Distance(g5,g8) = 2
    c: DistanceX(g9,g7) = 15
    c: Distance(g16,g2) = 4
    c: DistanceX(g4,g-1) = 7
    c: PointOnObject(g4,g2)
FEATURE [PartDesign::Pad] Pad022  label="strap001"
  BaseFeature = -> Pocket029
  Direction = (0,0,1)
  Length = 5
  Length2 = 10
  Profile = -> Sketch063
  ReferenceAxis = -> Sketch063 [N_Axis]
  Refine = true
  Suppressed = false
  Type = 0
FEATURE [Sketcher::SketchObject] Sketch064  label="on_off_grard_text"
  ArcFitTolerance = 1e-06
  AttachmentSupport = -> [XY_Plane053]
  ExternalTypes = [0,0]
  FullyConstrained = true
  MakeInternals = false
  MapMode = 5
  sketch-geometry (8):
    g0: LineSegment StartX=-3.99111 StartY=67.5 StartZ=0 EndX=-3.99111 EndY=57.5 EndZ=0
    g1: LineSegment StartX=-3.99111 StartY=57.5 StartZ=0 EndX=-1.99111 EndY=57.5 EndZ=0
    g2: LineSegment StartX=-1.99111 StartY=57.5 StartZ=0 EndX=-1.99111 EndY=67.5 EndZ=0
    g3: LineSegment StartX=-1.99111 StartY=67.5 StartZ=0 EndX=-3.99111 EndY=67.5 EndZ=0
    g4: GeomPoint [constr] X=-2.99111 Y=62.5 Z=0
    g5: GeomPoint X=-5.99111 Y=62.5 Z=0
    g6: GeomPoint X=8.00889 Y=62.5 Z=0
    g7: LineSegment [constr] StartX=-5.99111 StartY=62.5 StartZ=0 EndX=8.00889 EndY=62.5 EndZ=0
  constraints (17):
    c: Coincident(g0,g1)
    c: Coincident(g1,g2)
    c: Coincident(g2,g3)
    c: Coincident(g3,g0)
    c: Vertical(g0)
    c: Vertical(g2)
    c: Horizontal(g1)
    c: Horizontal(g3)
    c: Symmetric(g2,g0,g4)
    c: DistanceY(g0,g0) = 10
    c: DistanceX(g0,g2) = 2
    c: Symmetric(g-3,g-3,g5)
    c: Symmetric(g-4,g-4,g6)
    c: Coincident(g7,g5)
    c: Coincident(g7,g6)
    c: PointOnObject(g4,g7)
    c: Distance(g5,g0) = 2
FEATURE [PartDesign::Pocket] Pocket031  label="on_off_grard_text001"
  BaseFeature = -> Pad022
  Direction = (0,0,-1)
  Length = 0.4
  Length2 = 5
  Profile = -> Sketch064
  ReferenceAxis = -> Sketch064 [N_Axis]
  Refine = true
  Suppressed = false
  Type = 0
FEATURE [Sketcher::SketchObject] Sketch065  label="ble_antenna"
  ArcFitTolerance = 1e-06
  AttachmentOffset = pos=(0,0,-25) rot=(0,0,1;0rad)
  AttachmentSupport = -> [XY_Plane053]
  ExternalTypes = [0]
  FullyConstrained = true
  MakeInternals = false
  MapMode = 5
  Placement = pos=(0,0,-25) rot=(0,0,1;0rad)
  expr: .AttachmentOffset.Base.z = -VarSet.case_height
  expr: Constraints[3] = VarSet.base_width / 2 - 2.2 * VarSet.Base_case_thickness
  sketch-geometry (17):
    g0: LineSegment [constr] StartX=25.9 StartY=0 StartZ=0 EndX=25.9 EndY=60 EndZ=0
    g1: LineSegment StartX=25.9 StartY=45.5 StartZ=0 EndX=25.9 EndY=48.5 EndZ=0
    g2: LineSegment StartX=25.9 StartY=48.5 StartZ=0 EndX=20.9 EndY=48.5 EndZ=0
    g3: LineSegment StartX=20.9 StartY=48.5 StartZ=0 EndX=20.9 EndY=45.5 EndZ=0
    g4: LineSegment StartX=20.9 StartY=45.5 StartZ=0 EndX=22.4 EndY=45.5 EndZ=0
    g5: LineSegment StartX=22.4 StartY=45.5 StartZ=0 EndX=22.4 EndY=47 EndZ=0
    g6: LineSegment StartX=22.4 StartY=47 StartZ=0 EndX=24.4 EndY=47 EndZ=0
    g7: LineSegment StartX=24.4 StartY=47 StartZ=0 EndX=24.4 EndY=45.5 EndZ=0
    g8: LineSegment StartX=24.4 StartY=45.5 StartZ=0 EndX=25.9 EndY=45.5 EndZ=0
    g9: LineSegment StartX=25.9 StartY=8 StartZ=0 EndX=25.9 EndY=5 EndZ=0
    g10: LineSegment StartX=25.9 StartY=5 StartZ=0 EndX=20.9 EndY=5 EndZ=0
    g11: LineSegment StartX=20.9 StartY=5 StartZ=0 EndX=20.9 EndY=8 EndZ=0
    g12: LineSegment StartX=20.9 StartY=8 StartZ=0 EndX=22.4 EndY=8 EndZ=0
    g13: LineSegment StartX=22.4 StartY=8 StartZ=0 EndX=22.4 EndY=6.5 EndZ=0
    g14: LineSegment StartX=22.4 StartY=6.5 StartZ=0 EndX=24.4 EndY=6.5 EndZ=0
    g15: LineSegment StartX=24.4 StartY=6.5 StartZ=0 EndX=24.4 EndY=8 EndZ=0
    g16: LineSegment StartX=24.4 StartY=8 StartZ=0 EndX=25.9 EndY=8 EndZ=0
  constraints (52):
    c: Distance(g0) = 60
    c: Vertical(g0)
    c: PointOnObject(g0,g-1)
    c: Distance(g0,g-2) = 25.9
    c: Vertical(g1)
    c: Coincident(g1,g2)
    c: Horizontal(g2)
    c: Coincident(g2,g3)
    c: Vertical(g3)
    c: Coincident(g3,g4)
    c: Horizontal(g4)
    c: Coincident(g4,g5)
    c: Coincident(g5,g6)
    c: Horizontal(g6)
    c: Coincident(g6,g7)
    c: Vertical(g7)
    c: Coincident(g7,g8)
    c: Coincident(g1,g8)
    c: Perpendicular(g1,g8)
    c: DistanceX(g5,g6) = 2
    c: Perpendicular(g4,g5)
    c: DistanceY(g3,g2) = 3
    c: Distance(g4,g3) = 1.5
    c: Equal(g4,g5)
    c: Equal(g5,g7)
    c: Equal(g7,g8)
    c: PointOnObject(g1,g0)
    c: PointOnObject(g9,g0)
    c: PointOnObject(g9,g0)
    c: Coincident(g9,g10)
    c: Horizontal(g10)
    c: Coincident(g10,g11)
    c: Vertical(g11)
    c: Coincident(g11,g12)
    c: Horizontal(g12)
    c: Coincident(g12,g13)
    c: Vertical(g13)
    c: Coincident(g13,g14)
    c: Horizontal(g14)
    c: Coincident(g14,g15)
    c: Coincident(g15,g16)
    c: Coincident(g16,g9)
    c: Horizontal(g16)
    c: Parallel(g15,g0)
    c: Equal(g6,g14)
    c: Equal(g4,g12)
    c: Equal(g12,g13)
    c: Equal(g13,g15)
    c: Equal(g15,g16)
    c: Equal(g3,g11)
    c: DistanceY(g14,g6) = 40.5
    c: Distance(g9,g-1) = 5
FEATURE [PartDesign::Pad] Pad023  label="ble_antenna001"
  BaseFeature = -> Pocket031
  Direction = (0,0,1)
  Length = 12
  Length2 = 10
  Profile = -> Sketch065
  ReferenceAxis = -> Sketch065 [N_Axis]
  Refine = true
  Suppressed = false
  Type = 0
FEATURE [Sketcher::SketchObject] Sketch066  label="water_dranage"
  ArcFitTolerance = 1e-06
  AttachmentSupport = -> [XY_Plane053]
  ExternalGeometry = -> [Pad023]
  ExternalTypes = [0]
  FullyConstrained = true
  MakeInternals = false
  MapMode = 5
  sketch-geometry (3):
    g0: ArcOfCircle CenterX=17 CenterY=55 CenterZ=0 NormalX=0 NormalY=0 NormalZ=1 AngleXU=0 Radius=1 StartAngle=1.61e-14 EndAngle=3.14159
    g1: LineSegment StartX=16 StartY=55 StartZ=0 EndX=18 EndY=55 EndZ=0
    g2: GeomPoint X=17 Y=55 Z=0
  constraints (7):
    c: Coincident(g1,g0)
    c: Coincident(g1,g0)
    c: Horizontal(g1)
    c: PointOnObject(g0,g1)
    c: Symmetric(g-3,g-3,g2)
    c: Coincident(g0,g2)
    c: Radius(g0) = 1
FEATURE [PartDesign::Pocket] Pocket032  label="water_dranage001"
  BaseFeature = -> Pad023
  Direction = (0,0,-1)
  Length = 16
  Length2 = 5
  Profile = -> Sketch066
  ReferenceAxis = -> Sketch066 [N_Axis]
  Refine = true
  Suppressed = false
  Type = 0
FEATURE [PartDesign::PolarPattern] PolarPattern  label="water_dranage002"
  Angle = 360
  Axis = -> Pocket032 [Edge443]
  BaseFeature = -> Pocket032
  Mode = 0
  Occurrences = 3
  Offset = 120
  Originals = -> [Pocket032]
  Refine = true
  Suppressed = false
  TransformMode = 0
FEATURE [PartDesign::Fillet] Fillet006
  Base = -> PolarPattern [Edge476,Edge177,Edge172,Edge478]
  BaseFeature = -> PolarPattern
  Radius = 5
  Refine = true
  SupportTransform = false
  Suppressed = false
  UseAllEdges = false
FEATURE [PartDesign::Body] Body  label="main_body001"
  AllowCompound = false
  Group = -> [Sketch,Pad,Pocket,Pocket001,Sketch003,Pad002,Pocket002,Sketch004,Sketch005,Pocket007,Pocket008,Pocket010,Pad007,Sketch019,Sketch020,Pocket018,Sketch024,Pocket025,Sketch032,SubtractivePipe,Pocket028,Pad020,Sketch046,Pad021,Sketch047,Pocket029,Sketch063,Pad022,Sketch064,Pocket031,Sketch065,Pad023,Sketch066,Pocket032,PolarPattern,Fillet006]
  Origin = -> Origin106
  Tip = -> Fillet006
COMPONENT P9 — recipe-attached ("battery001", modeled in this document).
Construction recipe (the document's own serialized feature program — sketch geometry with constraints, then the solid features built on it; lengths are millimeters unless a unit is written):

FEATURE [Sketcher::SketchObject] Sketch006  label="battery_body001"
  ArcFitTolerance = 1e-06
  AttachmentSupport = -> [XY_Plane058]
  ExternalTypes = [0]
  FullyConstrained = true
  MakeInternals = false
  MapMode = 5
  expr: Constraints[13] = VarSet.base_width
  expr: Constraints[14] = VarSet.Base_battery_lenght
  expr: Constraints[30] = VarSet.Base_m3_insert
  expr: Constraints[44] = VarSet.Base_case_thickness
  expr: Constraints[47] = VarSet.Base_case_thickness + VarSet.Base_m3_insert / 2
  expr: Constraints[48] = VarSet.Base_case_thickness + VarSet.Base_m3_insert / 2
  expr: Constraints[67] = VarSet.Base_case_thickness / 2
  expr: Constraints[84] = VarSet.Base_case_thickness
  expr: Constraints[85] = VarSet.Base_case_thickness
  expr: Constraints[92] = VarSet.Base_case_thickness / 2
  sketch-geometry (40):
    g0: LineSegment StartX=-32.5 StartY=0 StartZ=0 EndX=32.5 EndY=0 EndZ=0
    g1: LineSegment StartX=32.5 StartY=0 StartZ=0 EndX=32.5 EndY=81 EndZ=0
    g2: LineSegment StartX=28.5 StartY=85 StartZ=0 EndX=-28.5 EndY=85 EndZ=0
    g3: LineSegment StartX=-32.5 StartY=81 StartZ=0 EndX=-32.5 EndY=0 EndZ=0
    g4: GeomPoint [constr] X=-32.5 Y=85 Z=0
    g5: ArcOfCircle CenterX=28.5 CenterY=81 CenterZ=0 NormalX=0 NormalY=0 NormalZ=1 AngleXU=0 Radius=4 StartAngle=1e-15 EndAngle=1.5708
    g6: GeomPoint [constr] X=32.5 Y=85 Z=0
    g7: Circle CenterX=-28.5 CenterY=4 CenterZ=0 NormalX=0 NormalY=0 NormalZ=1 AngleXU=0 Radius=1.6
    g8: Circle CenterX=28.5 CenterY=4 CenterZ=0 NormalX=0 NormalY=0 NormalZ=1 AngleXU=0 Radius=1.6
    g9: Circle CenterX=28.5 CenterY=81 CenterZ=0 NormalX=0 NormalY=0 NormalZ=1 AngleXU=0 Radius=1.6
    g10: Circle CenterX=-28.5 CenterY=81 CenterZ=0 NormalX=0 NormalY=0 NormalZ=1 AngleXU=0 Radius=1.6
    g11: LineSegment [constr] StartX=-28.5 StartY=81 StartZ=0 EndX=-28.5 EndY=4 EndZ=0
    g12: LineSegment [constr] StartX=-28.5 StartY=4 StartZ=0 EndX=28.5 EndY=4 EndZ=0
    g13: LineSegment [constr] StartX=28.5 StartY=4 StartZ=0 EndX=28.5 EndY=81 EndZ=0
    g14: LineSegment [constr] StartX=28.5 StartY=81 StartZ=0 EndX=-28.5 EndY=81 EndZ=0
    g15: LineSegment StartX=-24.01 StartY=82 StartZ=0 EndX=23.9076 EndY=82 EndZ=0
    g16: LineSegment StartX=29.5 StartY=76.4076 StartZ=0 EndX=29.5 EndY=8.48999 EndZ=0
    g17: LineSegment StartX=24.01 StartY=3 StartZ=0 EndX=-24.01 EndY=3 EndZ=0
    g18: LineSegment StartX=-29.5 StartY=8.48999 StartZ=0 EndX=-29.5 EndY=76.51 EndZ=0
    g19: ArcOfCircle CenterX=-28.5 CenterY=4 CenterZ=0 NormalX=0 NormalY=0 NormalZ=1 AngleXU=0 Radius=4.6 StartAngle=6.06404 EndAngle=8.07312
    g20: ArcOfCircle CenterX=-28.5 CenterY=81 CenterZ=0 NormalX=0 NormalY=0 NormalZ=1 AngleXU=0 Radius=4.6 StartAngle=4.49325 EndAngle=6.50233
    g21: ArcOfCircle CenterX=28.5 CenterY=81 CenterZ=0 NormalX=0 NormalY=0 NormalZ=1 AngleXU=0 Radius=4.7 StartAngle=2.92719 EndAngle=4.92679
    g22: ArcOfCircle CenterX=28.5 CenterY=4 CenterZ=0 NormalX=0 NormalY=0 NormalZ=1 AngleXU=0 Radius=4.6 StartAngle=1.35166 EndAngle=3.36073
    g23: ArcOfCircle CenterX=28.5 CenterY=4 CenterZ=0 NormalX=0 NormalY=0 NormalZ=1 AngleXU=0 Radius=3.1 StartAngle=1.35166 EndAngle=3.36073
    g24: ArcOfCircle CenterX=24.01 CenterY=3 CenterZ=0 NormalX=0 NormalY=0 NormalZ=1 AngleXU=-3.14159 Radius=1.5 StartAngle=1.5708 EndAngle=3.36073
    g25: LineSegment StartX=24.01 StartY=1.5 StartZ=0 EndX=-24.01 EndY=1.5 EndZ=0
    g26: ArcOfCircle CenterX=-24.01 CenterY=3 CenterZ=0 NormalX=0 NormalY=0 NormalZ=1 AngleXU=1.55119 Radius=1.5 StartAngle=1.37126 EndAngle=3.1612
    g27: ArcOfCircle CenterX=-28.5 CenterY=4 CenterZ=0 NormalX=0 NormalY=0 NormalZ=1 AngleXU=0 Radius=3.1 StartAngle=6.06404 EndAngle=8.07312
    g28: ArcOfCircle CenterX=-29.5 CenterY=8.48999 CenterZ=0 NormalX=0 NormalY=0 NormalZ=1 AngleXU=1.5708 Radius=1.5 StartAngle=1.5708 EndAngle=3.36073
    g29: LineSegment StartX=-31 StartY=8.48999 StartZ=0 EndX=-31 EndY=76.51 EndZ=0
    g30: ArcOfCircle CenterX=-29.5 CenterY=76.51 CenterZ=0 NormalX=0 NormalY=0 NormalZ=1 AngleXU=-0.0196091 Radius=1.5 StartAngle=1.37126 EndAngle=3.1612
    g31: ArcOfCircle CenterX=-28.5 CenterY=81 CenterZ=0 NormalX=0 NormalY=0 NormalZ=1 AngleXU=0 Radius=3.1 StartAngle=4.49325 EndAngle=6.50233
    g32: ArcOfCircle CenterX=-24.01 CenterY=82 CenterZ=0 NormalX=0 NormalY=0 NormalZ=1 AngleXU=0 Radius=1.5 StartAngle=1.5708 EndAngle=3.36073
    g33: LineSegment StartX=-24.01 StartY=83.5 StartZ=0 EndX=23.9076 EndY=83.5 EndZ=0
    g34: ArcOfCircle CenterX=23.9076 CenterY=82 CenterZ=0 NormalX=0 NormalY=0 NormalZ=1 AngleXU=-1.5708 Radius=1.5 StartAngle=1.35639 EndAngle=3.14159
    g35: ArcOfCircle CenterX=28.5 CenterY=81 CenterZ=0 NormalX=0 NormalY=0 NormalZ=1 AngleXU=0 Radius=3.2 StartAngle=2.92719 EndAngle=4.92679
    g36: ArcOfCircle CenterX=29.5 CenterY=76.4076 CenterZ=0 NormalX=0 NormalY=0 NormalZ=1 AngleXU=-1.5708 Radius=1.5 StartAngle=1.5708 EndAngle=3.356
    g37: LineSegment StartX=31 StartY=76.4076 StartZ=0 EndX=31 EndY=8.48999 EndZ=0
    g38: ArcOfCircle CenterX=29.5 CenterY=8.48999 CenterZ=0 NormalX=0 NormalY=0 NormalZ=1 AngleXU=3.12198 Radius=1.5 StartAngle=1.37126 EndAngle=3.1612
    g39: ArcOfCircle CenterX=-28.5 CenterY=81 CenterZ=0 NormalX=0 NormalY=0 NormalZ=1 AngleXU=0 Radius=4 StartAngle=1.5708 EndAngle=3.14159
  constraints (94):
    c: Coincident(g0,g1)
    c: Coincident(g3,g0)
    c: Horizontal(g2)
    c: Vertical(g1)
    c: Vertical(g3)
    c: PointOnObject(g0,g-1)
    c: Symmetric(g0,g0,g-2)
    c: PointOnObject(g4,g3)
    c: PointOnObject(g4,g2)
    c: PointOnObject(g6,g1)
    c: PointOnObject(g6,g2)
    c: Tangent(g1,g5) = -1.5708
    c: Tangent(g2,g5) = -1.5708
    c: DistanceX(g4,g6) = 65
    c: DistanceY(g0,g4) = 85
    c: Coincident(g11,g12)
    c: Coincident(g12,g13)
    c: Coincident(g13,g14)
    c: Coincident(g14,g11)
    c: Vertical(g11)
    c: Vertical(g13)
    c: Horizontal(g12)
    c: Coincident(g11,g10)
    c: Coincident(g12,g8)
    c: Coincident(g7,g11)
    c: Coincident(g13,g9)
    c: Symmetric(g10,g9,g-2)
    c: Equal(g10,g9)
    c: Equal(g9,g8)
    c: Equal(g8,g7)
    c: Diameter(g10) = 3.2
    c: Distance(g7,g0) = 2.4
    c: Horizontal(g15)
    c: Vertical(g16)
    c: Horizontal(g17)
    c: Vertical(g18)
    c: Coincident(g19,g18)
    c: Coincident(g19,g17)
    c: Coincident(g20,g18)
    c: Coincident(g20,g15)
    c: Coincident(g21,g15)
    c: Coincident(g21,g16)
    c: Coincident(g22,g16)
    c: Coincident(g22,g17)
    c: Distance(g17,g0) = 3
    c: Coincident(g22,g8)
    c: Coincident(g19,g7)
    c: Radius(g19) = 4.6
    c: Radius(g20) = 4.6
    c: Coincident(g10,g20)
    c: Coincident(g21,g5)
    c: Tangent(g23,g24) = 1.5708
    c: Tangent(g23,g38) = 1.5708
    c: Tangent(g24,g25) = 1.5708
    c: Tangent(g25,g26) = 1.5708
    c: Tangent(g26,g27) = 1.5708
    c: Tangent(g27,g28) = 1.5708
    c: Tangent(g28,g29) = 1.5708
    c: Tangent(g29,g30) = 1.5708
    c: Tangent(g30,g31) = 1.5708
    c: Tangent(g31,g32) = 1.5708
    c: Tangent(g32,g33) = 1.5708
    c: Tangent(g33,g34) = 1.5708
    c: Tangent(g34,g35) = 1.5708
    c: Tangent(g35,g36) = 1.5708
    c: Tangent(g36,g37) = 1.5708
    c: Tangent(g37,g38) = 1.5708
    c: Distance(g17,g25) = 1.5
    c: Coincident(g32,g15)
    c: Coincident(g30,g18)
    c: Coincident(g36,g16)
    c: Coincident(g24,g17)
    c: Coincident(g26,g17)
    c: Coincident(g28,g18)
    c: Coincident(g27,g7)
    c: Coincident(g23,g8)
    c: Coincident(g9,g35)
    c: Coincident(g34,g15)
    c: Coincident(g38,g16)
    c: Coincident(g39,g10)
    c: Coincident(g39,g2)
    c: Coincident(g39,g3)
    c: Coincident(g31,g10)
    c: Coincident(g5,g9)
    c: Distance(g1,g16) = 3
    c: Distance(g18,g3) = 3
    c: Parallel(g25,g-1)
    c: Parallel(g29,g-2)
    c: Parallel(g33,g-1)
    c: Equal(g27,g23)
    c: Distance(g10,g2) = 2.4
    c: Radius(g39) = 4
    c: Distance(g33,g2) = 1.5
    c: Radius(g35) = 3.2
FEATURE [PartDesign::Pad] Pad004
  Direction = (0,0,1)
  Length = 25
  Length2 = 10
  Profile = -> Sketch006 [Edge1,Edge6,Edge5,Edge4,Edge3,Edge2]
  ReferenceAxis = -> Sketch006 [N_Axis]
  Refine = true
  Reversed = true
  Suppressed = false
  Type = 0
  expr: Length = VarSet.case_height
FEATURE [PartDesign::Pocket] Pocket005  label="pocket"
  BaseFeature = -> Pad004
  Direction = (0,0,-1)
  Length = 22
  Length2 = 5
  Profile = -> Sketch006 [Edge15,Edge16,Edge17,Edge18,Edge11,Edge12,Edge13,Edge14]
  ReferenceAxis = -> Sketch006 [N_Axis]
  Refine = true
  Suppressed = false
  Type = 0
  expr: Length = VarSet.case_height - VarSet.Base_case_thickness
FEATURE [PartDesign::Pocket] Pocket006  label="screw001"
  BaseFeature = -> Pocket005
  Direction = (0,0,-1)
  Length = 5
  Length2 = 5
  Midplane = true
  Profile = -> Sketch006 [Edge10,Edge9,Edge8,Edge7]
  ReferenceAxis = -> Sketch006 [N_Axis]
  Refine = true
  Suppressed = false
  Type = 1
FEATURE [Sketcher::SketchObject] Sketch007  label="18650_battery_holder"
  ArcFitTolerance = 1e-06
  AttachmentOffset = pos=(0,0,-21) rot=(0,0,1;0rad)
  AttachmentSupport = -> [XZ_Plane058]
  ExternalGeometry = -> [Pocket006]
  ExternalTypes = [0,0,0]
  FullyConstrained = true
  MakeInternals = false
  MapMode = 5
  Placement = pos=(0,21,-4.7e-15) rot=(1,0,0;1.5708rad)
  expr: .AttachmentOffset.Base.z = -7 * VarSet.Base_case_thickness
  sketch-geometry (12):
    g0: ArcOfCircle CenterX=-19.4 CenterY=-12 CenterZ=0 NormalX=0 NormalY=0 NormalZ=1 AngleXU=0 Radius=9.5 StartAngle=3.14159 EndAngle=6.28319
    g1: LineSegment StartX=-28.9 StartY=-12 StartZ=0 EndX=-29.4 EndY=-12 EndZ=0
    g2: LineSegment StartX=-29.4 StartY=-12 StartZ=0 EndX=-29.4 EndY=-22 EndZ=0
    g3: LineSegment StartX=-29.4 StartY=-22 StartZ=0 EndX=29.5 EndY=-22 EndZ=0
    g4: LineSegment StartX=-9.4 StartY=-12 StartZ=0 EndX=-9.9 EndY=-12 EndZ=0
    g5: LineSegment [constr] StartX=-29.4 StartY=-12 StartZ=0 EndX=29.5 EndY=-12 EndZ=0
    g6: LineSegment [constr] StartX=29.5 StartY=0 StartZ=0 EndX=29.5 EndY=-12 EndZ=0
    g7: ArcOfCircle CenterX=0.1 CenterY=-12 CenterZ=0 NormalX=0 NormalY=0 NormalZ=1 AngleXU=0 Radius=9.5 StartAngle=3.14159 EndAngle=6.28319
    g8: LineSegment StartX=9.6 StartY=-12 StartZ=0 EndX=10.1 EndY=-12 EndZ=0
    g9: ArcOfCircle CenterX=19.6 CenterY=-12 CenterZ=0 NormalX=0 NormalY=0 NormalZ=1 AngleXU=0 Radius=9.5 StartAngle=3.14159 EndAngle=6.28319
    g10: LineSegment StartX=29.1 StartY=-12 StartZ=0 EndX=29.5 EndY=-12 EndZ=0
    g11: LineSegment StartX=29.5 StartY=-22 StartZ=0 EndX=29.5 EndY=-12 EndZ=0
  constraints (37):
    c: Coincident(g1,g2)
    c: Vertical(g2)
    c: Coincident(g2,g3)
    c: Horizontal(g3)
    c: Coincident(g0,g1)
    c: Radius(g0) = 9.5
    c: DistanceY(g2,g1) = 10
    c: PointOnObject(g3,g-3)
    c: DistanceX(g1,g0) = 0.5
    c: DistanceX(g-5,g1) = 0.1
    c: Coincident(g4,g0)
    c: Horizontal(g4)
    c: Coincident(g5,g1)
    c: Horizontal(g5)
    c: Coincident(g6,g-4)
    c: Coincident(g6,g5)
    c: Vertical(g6)
    c: PointOnObject(g7,g5)
    c: Coincident(g7,g4)
    c: PointOnObject(g7,g5)
    c: Coincident(g7,g8)
    c: PointOnObject(g8,g5)
    c: PointOnObject(g0,g5)
    c: PointOnObject(g0,g5)
    c: PointOnObject(g0,g5)
    c: PointOnObject(g9,g5)
    c: Coincident(g9,g8)
    c: PointOnObject(g9,g5)
    c: Coincident(g10,g9)
    c: Coincident(g11,g3)
    c: Coincident(g11,g10)
    c: Perpendicular(g11,g3)
    c: Equal(g1,g4)
    c: Equal(g4,g8)
    c: Equal(g0,g7)
    c: Equal(g7,g9)
    c: Coincident(g10,g5)
FEATURE [PartDesign::Pad] Pad005  label="18650_battery_holder001"
  BaseFeature = -> Pocket006
  Direction = (0,-1,2e-16)
  Length = 5
  Length2 = 10
  Midplane = true
  Profile = -> Sketch007
  ReferenceAxis = -> Sketch007 [N_Axis]
  Refine = true
  Suppressed = false
  Type = 0
FEATURE [Sketcher::SketchObject] Sketch011  label="main_lunges"
  ArcFitTolerance = 1e-06
  AttachmentSupport = -> [XZ_Plane065]
  ExternalTypes = [0]
  FullyConstrained = true
  MakeInternals = false
  MapMode = 5
  Placement = pos=(0,0,0) rot=(1,0,0;1.5708rad)
  expr: Constraints[10] = VarSet.case_height
  expr: Constraints[12] = VarSet.case_height / 2
  expr: Constraints[17] = VarSet.Base_connector_bounting_box_height
  expr: Constraints[36] = VarSet.Base_connector_lug_remaining_key
  expr: Constraints[37] = VarSet.Base_connector_lug_remaining_key
  expr: Constraints[40] = VarSet.Base_connector_external_lug - VarSet.Base_connector_lug_offset
  expr: Constraints[42] = VarSet.Base_connector_internal_lug + VarSet.Base_connector_lug_offset
  expr: Constraints[46] = VarSet.Base_connector_internal_lug + VarSet.Base_connecot_lug_multipl * VarSet.Base_connector_lug_offset
  expr: Constraints[47] = VarSet.Base_connector_external_lug - VarSet.Base_connecot_lug_multipl * VarSet.Base_connector_lug_offset
  expr: Constraints[9] = VarSet.base_width
  sketch-geometry (24):
    g0: LineSegment [constr] StartX=-32.5 StartY=0 StartZ=0 EndX=-32.5 EndY=-25 EndZ=0
    g1: LineSegment [constr] StartX=-32.5 StartY=-25 StartZ=0 EndX=32.5 EndY=-25 EndZ=0
    g2: LineSegment [constr] StartX=32.5 StartY=-25 StartZ=0 EndX=32.5 EndY=0 EndZ=0
    g3: LineSegment [constr] StartX=32.5 StartY=0 StartZ=0 EndX=-32.5 EndY=0 EndZ=0
    g4: GeomPoint X=0 Y=-12.5 Z=0
    g5: LineSegment [constr] StartX=-32.5 StartY=-1.5 StartZ=0 EndX=32.5 EndY=-1.5 EndZ=0
    g6: LineSegment [constr] StartX=-32.5 StartY=-23.5 StartZ=0 EndX=32.5 EndY=-23.5 EndZ=0
    g7: LineSegment [constr] StartX=-32.5 StartY=-1.5 StartZ=0 EndX=32.5 EndY=-23.5 EndZ=0
    g8: LineSegment StartX=5.04083 StartY=-23.5 StartZ=0 EndX=15.3691 EndY=-23.5 EndZ=0
    g9: LineSegment StartX=11.1283 StartY=-7.5 StartZ=0 EndX=18.1229 EndY=-7.5 EndZ=0
    g10: LineSegment StartX=-15.3691 StartY=-1.5 StartZ=0 EndX=-5.04083 EndY=-1.5 EndZ=0
    g11: LineSegment StartX=-18.1229 StartY=-17.5 StartZ=0 EndX=-11.1283 EndY=-17.5 EndZ=0
    g12: LineSegment StartX=-32.5 StartY=-1.5 StartZ=0 EndX=-32.5 EndY=-23.5 EndZ=0
    g13: LineSegment StartX=-32.5 StartY=-23.5 StartZ=0 EndX=32.5 EndY=-23.5 EndZ=0
    g14: LineSegment StartX=32.5 StartY=-23.5 StartZ=0 EndX=32.5 EndY=-1.5 EndZ=0
    g15: LineSegment StartX=32.5 StartY=-1.5 StartZ=0 EndX=-32.5 EndY=-1.5 EndZ=0
    g16: Circle [constr] CenterX=0 CenterY=-12.5 CenterZ=0 NormalX=0 NormalY=0 NormalZ=1 AngleXU=0 Radius=18.9
    g17: Circle [constr] CenterX=0 CenterY=-12.5 CenterZ=0 NormalX=0 NormalY=0 NormalZ=1 AngleXU=0 Radius=12.1
    g18: Circle [constr] CenterX=0 CenterY=-12.5 CenterZ=0 NormalX=0 NormalY=0 NormalZ=1 AngleXU=0 Radius=12.2
    g19: Circle [constr] CenterX=0 CenterY=-12.5 CenterZ=0 NormalX=0 NormalY=0 NormalZ=1 AngleXU=0 Radius=18.8
    g20: ArcOfCircle CenterX=0.262977 CenterY=-12.4274 CenterZ=0 NormalX=0 NormalY=0 NormalZ=1 AngleXU=0 Radius=19.0728 StartAngle=2.53151 EndAngle=3.41079
    g21: ArcOfCircle CenterX=0.216708 CenterY=-12.6551 CenterZ=0 NormalX=0 NormalY=0 NormalZ=1 AngleXU=0 Radius=18.6335 StartAngle=5.66199 EndAngle=6.5635
    g22: ArcOfCircle CenterX=0 CenterY=-12.5759 CenterZ=0 NormalX=0 NormalY=0 NormalZ=1 AngleXU=0 Radius=12.1691 StartAngle=1.9979 EndAngle=3.55817
    g23: ArcOfCircle CenterX=0 CenterY=-12.4241 CenterZ=0 NormalX=0 NormalY=0 NormalZ=1 AngleXU=0 Radius=12.1691 StartAngle=5.13949 EndAngle=6.69977
  constraints (68):
    c: Coincident(g0,g1)
    c: Coincident(g1,g2)
    c: Coincident(g2,g3)
    c: Coincident(g3,g0)
    c: Vertical(g0)
    c: Vertical(g2)
    c: Horizontal(g1)
    c: PointOnObject(g0,g-1)
    c: Symmetric(g0,g2,g-2)
    c: DistanceX(g0,g2) = 65
    c: DistanceY(g0,g-1) = 25
    c: PointOnObject(g4,g-2)
    c: DistanceY(g4,g-1) = 12.5
    c: PointOnObject(g6,g0)
    c: Horizontal(g6)
    c: PointOnObject(g6,g2)
    c: PointOnObject(g5,g2)
    c: DistanceY(g6,g5) = 22
    c: PointOnObject(g5,g0)
    c: Parallel(g5,g3)
    c: Coincident(g7,g5)
    c: Coincident(g7,g6)
    c: PointOnObject(g4,g7)
    c: Parallel(g9,g3)
    c: Parallel(g11,g5)
    c: Coincident(g12,g13)
    c: Coincident(g13,g14)
    c: Coincident(g14,g15)
    c: Coincident(g15,g12)
    c: Vertical(g12)
    c: Horizontal(g13)
    c: Symmetric(g12,g14,g-2)
    c: Parallel(g10,g3)
    c: Parallel(g8,g6)
    c: Coincident(g12,g5)
    c: PointOnObject(g8,g13)
    c: Distance(g9,g15) = 6
    c: Distance(g11,g13) = 6
    c: Coincident(g16,g4)
    c: PointOnObject(g10,g16)
    c: Radius(g16) = 18.9
    c: Coincident(g17,g4)
    c: Radius(g17) = 12.1
    c: PointOnObject(g8,g16)
    c: Coincident(g18,g4)
    c: Coincident(g19,g4)
    c: Radius(g18) = 12.2
    c: Radius(g19) = 18.8
    c: PointOnObject(g11,g19)
    c: PointOnObject(g9,g19)
    c: Coincident(g20,g10)
    c: Coincident(g20,g11)
    c: Tangent(g20,g19)
    c: Coincident(g21,g9)
    c: Coincident(g21,g8)
    c: Tangent(g21,g16)
    c: Coincident(g13,g6)
    c: Coincident(g22,g10)
    c: Coincident(g22,g11)
    c: PointOnObject(g22,g-2)
    c: PointOnObject(g8,g17)
    c: PointOnObject(g9,g18)
    c: Coincident(g23,g8)
    c: Coincident(g23,g9)
    c: PointOnObject(g23,g-2)
    c: PointOnObject(g10,g15)
    c: PointOnObject(g10,g17)
    c: PointOnObject(g11,g18)
FEATURE [PartDesign::Pad] Pad008
  Direction = (0,-1,2e-16)
  Length = 1.5
  Length2 = 10
  Placement = pos=(0,0,0) rot=(1,0,0;1.5708rad)
  Profile = -> Sketch011 [Edge9,Edge12,Edge10,Edge11]
  ReferenceAxis = -> Sketch011 [N_Axis]
  Refine = true
  Reversed = true
  Suppressed = false
  Type = 0
  expr: Length = VarSet.Base_pogopin_cutout_height
FEATURE [PartDesign::Pad] Pad009
  BaseFeature = -> Pad008
  Direction = (0,-1,2e-16)
  Length = 12
  Length2 = 10
  Placement = pos=(0,0,0) rot=(1,0,0;1.5708rad)
  Profile = -> Sketch011 [Edge1,Edge4,Edge3,Edge2,Edge8,Edge7,Edge6,Edge5]
  ReferenceAxis = -> Sketch011 [N_Axis]
  Refine = true
  Suppressed = false
  Type = 0
  expr: Length = VarSet.Base_connector_height_lug
FEATURE [Sketcher::SketchObject] Sketch012  label="luges_cutting"
  ArcFitTolerance = 1e-06
  AttachmentSupport = -> [XZ_Plane065]
  ExternalTypes = [0]
  FullyConstrained = true
  MakeInternals = false
  MapMode = 5
  Placement = pos=(0,0,0) rot=(1,0,0;1.5708rad)
  expr: Constraints[11] = VarSet.Base_connector_bounting_box_height
  expr: Constraints[21] = VarSet.Base_connector_lug_remaining_key - VarSet.Base_connector_lug_offset
  expr: Constraints[22] = VarSet.Base_connector_lug_remaining_key - VarSet.Base_connector_lug_offset
  expr: Constraints[26] = (VarSet.Base_connector_external_lug + VarSet.Base_connector_internal_lug) / 2 + VarSet.Base_connector_lug_offset
  expr: Constraints[27] = (VarSet.Base_connector_external_lug + VarSet.Base_connector_internal_lug) / 2 - VarSet.Base_connecot_lug_multipl * VarSet.Base_connector_lug_offset
  expr: Constraints[28] = VarSet.Base_connector_internal_lug - VarSet.Base_connecot_lug_multipl * VarSet.Base_connector_lug_offset
  expr: Constraints[3] = VarSet.base_width
  expr: Constraints[6] = VarSet.case_height / 2
  sketch-geometry (17):
    g0: LineSegment [constr] StartX=-32.5 StartY=-1.5 StartZ=0 EndX=-32.5 EndY=-23.5 EndZ=0
    g1: LineSegment [constr] StartX=-32.5 StartY=-23.5 StartZ=0 EndX=32.5 EndY=-23.5 EndZ=0
    g2: LineSegment [constr] StartX=32.5 StartY=-23.5 StartZ=0 EndX=32.5 EndY=-1.5 EndZ=0
    g3: GeomPoint X=0 Y=-12.5 Z=0
    g4: LineSegment [constr] StartX=-32.5 StartY=-12.5 StartZ=0 EndX=32.5 EndY=-12.5 EndZ=0
    g5: LineSegment StartX=10.641 StartY=-17.6 StartZ=0 EndX=14.425 EndY=-17.6 EndZ=0
    g6: LineSegment [constr] StartX=-32.5 StartY=-1.5 StartZ=0 EndX=32.5 EndY=-1.5 EndZ=0
    g7: LineSegment StartX=-14.425 StartY=-7.4 StartZ=0 EndX=-10.641 EndY=-7.4 EndZ=0
    g8: LineSegment StartX=-4.27083 StartY=-23.5 StartZ=0 EndX=-11.0616 EndY=-23.5 EndZ=0
    g9: LineSegment StartX=4.27083 StartY=-1.5 StartZ=0 EndX=11.0616 EndY=-1.5 EndZ=0
    g10: Circle [constr] CenterX=0 CenterY=-12.5 CenterZ=0 NormalX=0 NormalY=0 NormalZ=1 AngleXU=0 Radius=15.3
    g11: Circle [constr] CenterX=0 CenterY=-12.5 CenterZ=0 NormalX=0 NormalY=0 NormalZ=1 AngleXU=0 Radius=11.8
    g12: Circle [constr] CenterX=0 CenterY=-12.5 CenterZ=0 NormalX=0 NormalY=0 NormalZ=1 AngleXU=0 Radius=15.6
    g13: ArcOfCircle CenterX=0 CenterY=-12.5 CenterZ=0 NormalX=0 NormalY=0 NormalZ=1 AngleXU=0 Radius=11.8 StartAngle=5.83625 EndAngle=7.48364
    g14: ArcOfCircle CenterX=0 CenterY=-12.2121 CenterZ=0 NormalX=0 NormalY=0 NormalZ=1 AngleXU=0 Radius=15.3984 StartAngle=5.92572 EndAngle=7.05253
    g15: ArcOfCircle CenterX=0 CenterY=-12.5 CenterZ=0 NormalX=0 NormalY=0 NormalZ=1 AngleXU=0 Radius=11.8 StartAngle=2.69466 EndAngle=4.34205
    g16: ArcOfCircle CenterX=0 CenterY=-12.7879 CenterZ=0 NormalX=0 NormalY=0 NormalZ=1 AngleXU=0 Radius=15.3984 StartAngle=2.78413 EndAngle=3.91094
  constraints (49):
    c: Vertical(g0)
    c: Vertical(g2)
    c: Horizontal(g1)
    c: DistanceX(g0,g2) = 65
    c: Symmetric(g0,g2,g-2)
    c: PointOnObject(g3,g-2)
    c: DistanceY(g3,g-1) = 12.5
    c: Symmetric(g0,g0,g4)
    c: Symmetric(g2,g2,g4)
    c: Coincident(g1,g2)
    c: Coincident(g1,g0)
    c: DistanceY(g1,g2) = 22
    c: Coincident(g6,g0)
    c: Coincident(g6,g2)
    c: PointOnObject(g3,g4)
    c: PointOnObject(g9,g6)
    c: PointOnObject(g8,g1)
    c: PointOnObject(g8,g1)
    c: PointOnObject(g9,g6)
    c: Parallel(g7,g6)
    c: Parallel(g1,g5)
    c: Distance(g7,g6) = 5.9
    c: Distance(g5,g1) = 5.9
    c: Coincident(g10,g3)
    c: Coincident(g11,g3)
    c: Coincident(g12,g3)
    c: Radius(g12) = 15.6
    c: Radius(g10) = 15.3
    c: Radius(g11) = 11.8
    c: PointOnObject(g8,g12)
    c: PointOnObject(g8,g11)
    c: PointOnObject(g9,g12)
    c: PointOnObject(g9,g11)
    c: PointOnObject(g5,g10)
    c: Coincident(g13,g9)
    c: Coincident(g13,g5)
    c: PointOnObject(g13,g-2)
    c: Coincident(g14,g9)
    c: Coincident(g14,g5)
    c: PointOnObject(g14,g-2)
    c: PointOnObject(g7,g10)
    c: Coincident(g15,g8)
    c: Coincident(g15,g7)
    c: Coincident(g16,g7)
    c: Coincident(g16,g8)
    c: PointOnObject(g16,g-2)
    c: PointOnObject(g15,g-2)
    c: PointOnObject(g7,g11)
    c: PointOnObject(g5,g11)
FEATURE [PartDesign::Pocket] Pocket012
  BaseFeature = -> Pad009
  Direction = (0,1,-2e-16)
  Length = 6.7
  Length2 = 5
  Placement = pos=(0,0,0) rot=(1,0,0;1.5708rad)
  Profile = -> Sketch012
  ReferenceAxis = -> Sketch012 [N_Axis]
  Refine = true
  Reversed = true
  Suppressed = false
  Type = 0
  expr: Length = VarSet.Base_connector_height_lug / 2 + 5 * VarSet.Base_connector_lug_offset + VarSet.Base_connector_oring_offset
FEATURE [Sketcher::SketchObject] Sketch018  label="pogopins_case001"
  ArcFitTolerance = 1e-06
  AttachmentSupport = -> [XZ_Plane065]
  ExternalTypes = [0]
  FullyConstrained = true
  MakeInternals = false
  MapMode = 5
  Placement = pos=(0,0,0) rot=(1,0,0;1.5708rad)
  expr: Constraints[12] = VarSet.Base_pogopins_r
  expr: Constraints[1] = VarSet.case_height / 2
  expr: Constraints[25] = VarSet.Base_pogoping_lenght
  sketch-geometry (11):
    g0: GeomPoint X=0 Y=-12.5 Z=0
    g1: ArcOfCircle CenterX=-5.45 CenterY=-12.5 CenterZ=0 NormalX=0 NormalY=0 NormalZ=1 AngleXU=0 Radius=2.1 StartAngle=1.5708 EndAngle=4.71239
    g2: ArcOfCircle CenterX=5.45 CenterY=-12.5 CenterZ=0 NormalX=0 NormalY=0 NormalZ=1 AngleXU=0 Radius=2.1 StartAngle=4.71239 EndAngle=7.85398
    g3: LineSegment StartX=-5.45 StartY=-10.4 StartZ=0 EndX=5.45 EndY=-10.4 EndZ=0
    g4: LineSegment StartX=-5.45 StartY=-14.6 StartZ=0 EndX=5.45 EndY=-14.6 EndZ=0
    g5: LineSegment [constr] StartX=-5.45 StartY=-12.5 StartZ=0 EndX=5.45 EndY=-12.5 EndZ=0
    g6: GeomPoint [constr] X=0 Y=-12.5 Z=0
    g7: LineSegment [constr] StartX=-7.55 StartY=-10.4 StartZ=0 EndX=-7.55 EndY=-14.6 EndZ=0
    g8: LineSegment [constr] StartX=-7.55 StartY=-14.6 StartZ=0 EndX=7.55 EndY=-14.6 EndZ=0
    g9: LineSegment [constr] StartX=7.55 StartY=-14.6 StartZ=0 EndX=7.55 EndY=-10.4 EndZ=0
    g10: LineSegment [constr] StartX=7.55 StartY=-10.4 StartZ=0 EndX=-7.55 EndY=-10.4 EndZ=0
  constraints (26):
    c: PointOnObject(g0,g-2)
    c: Distance(g0,g-1) = 12.5
    c: Tangent(g1,g3) = 1.5708
    c: Tangent(g1,g4) = -1.5708
    c: Tangent(g2,g3) = 1.5708
    c: Tangent(g2,g4) = -1.5708
    c: Equal(g1,g2)
    c: Horizontal(g3)
    c: Coincident(g5,g1)
    c: Coincident(g5,g2)
    c: Symmetric(g5,g5,g6)
    c: Coincident(g0,g6)
    c: Radius(g1) = 2.1
    c: Coincident(g7,g8)
    c: Coincident(g8,g9)
    c: Coincident(g9,g10)
    c: Coincident(g10,g7)
    c: Vertical(g7)
    c: Vertical(g9)
    c: Horizontal(g8)
    c: Horizontal(g10)
    c: PointOnObject(g2,g10)
    c: PointOnObject(g2,g8)
    c: Tangent(g2,g9)
    c: Tangent(g7,g1)
    c: DistanceX(g7,g9) = 15.1
FEATURE [PartDesign::Pocket] Pocket016  label="pogopins"
  BaseFeature = -> Pocket012
  Direction = (0,1,-2e-16)
  Length = 12
  Length2 = 5
  Midplane = true
  Placement = pos=(0,0,0) rot=(1,0,0;1.5708rad)
  Profile = -> Sketch018
  ReferenceAxis = -> Sketch018 [N_Axis]
  Refine = true
  Suppressed = false
  Type = 0
  expr: Length = VarSet.Base_connector_height_lug
FEATURE [Sketcher::SketchObject] Sketch022  label="pogopins_outside"
  ArcFitTolerance = 1e-06
  ExternalTypes = [0]
  FullyConstrained = true
  MakeInternals = false
  MapMode = 5
  Placement = pos=(0,3,0) rot=(0,0.707107,0.707107;3.14159rad)
  expr: Constraints[11] = VarSet.case_height / 2
  expr: Constraints[12] = VarSet.Base_pogopin_outside
  expr: Constraints[13] = 3 * VarSet.Base_pogopins_r
  sketch-geometry (6):
    g0: GeomPoint X=0 Y=-12.5 Z=0
    g1: LineSegment StartX=-10.5 StartY=-9.35 StartZ=0 EndX=-10.5 EndY=-15.65 EndZ=0
    g2: LineSegment StartX=-10.5 StartY=-15.65 StartZ=0 EndX=10.5 EndY=-15.65 EndZ=0
    g3: LineSegment StartX=10.5 StartY=-15.65 StartZ=0 EndX=10.5 EndY=-9.35 EndZ=0
    g4: LineSegment StartX=10.5 StartY=-9.35 StartZ=0 EndX=-10.5 EndY=-9.35 EndZ=0
    g5: GeomPoint [constr] X=0 Y=-12.5 Z=0
  constraints (14):
    c: PointOnObject(g0,g-2)
    c: Coincident(g1,g2)
    c: Coincident(g2,g3)
    c: Coincident(g3,g4)
    c: Coincident(g4,g1)
    c: Vertical(g1)
    c: Vertical(g3)
    c: Horizontal(g2)
    c: Horizontal(g4)
    c: Symmetric(g3,g1,g5)
    c: Coincident(g5,g0)
    c: DistanceY(g0,g-1) = 12.5
    c: DistanceX(g1,g3) = 21
    c: DistanceY(g2,g3) = 6.3
FEATURE [PartDesign::Pocket] Pocket020
  BaseFeature = -> Pad005
  Direction = (-1e-16,-1,2e-16)
  Length = 3
  Length2 = 5
  Profile = -> Sketch022
  ReferenceAxis = -> Sketch022 [N_Axis]
  Refine = true
  Suppressed = false
  Type = 0
  expr: Length = VarSet.Base_case_thickness
FEATURE [Sketcher::SketchObject] Sketch033
  ArcFitTolerance = 1e-06
  AttachmentSupport = -> [YZ_Plane058]
  ExternalGeometry = -> [Sketch006]
  ExternalTypes = [0]
  FullyConstrained = true
  MakeInternals = false
  MapMode = 5
  Placement = pos=(0,0,0) rot=(0.57735,0.57735,0.57735;2.0944rad)
  expr: Constraints[10] = VarSet.Base_gasket_width
  expr: Constraints[11] = VarSet.Base_gasket_height
  sketch-geometry (5):
    g0: LineSegment StartX=1 StartY=1 StartZ=0 EndX=1 EndY=-1 EndZ=0
    g1: LineSegment StartX=1 StartY=-1 StartZ=0 EndX=2 EndY=-1 EndZ=0
    g2: LineSegment StartX=2 StartY=-1 StartZ=0 EndX=2 EndY=1 EndZ=0
    g3: LineSegment StartX=2 StartY=1 StartZ=0 EndX=1 EndY=1 EndZ=0
    g4: GeomPoint [constr] X=1.5 Y=0 Z=0
  constraints (12):
    c: Coincident(g0,g1)
    c: Coincident(g1,g2)
    c: Coincident(g2,g3)
    c: Coincident(g3,g0)
    c: Vertical(g0)
    c: Vertical(g2)
    c: Horizontal(g1)
    c: Horizontal(g3)
    c: Symmetric(g2,g0,g4)
    c: Coincident(g4,g-3)
    c: DistanceX(g0,g2) = 1
    c: DistanceY(g0,g0) = 2
FEATURE [PartDesign::SubtractivePipe] SubtractivePipe001  label="gasket_"
  AuxilleryCurvelinear = true
  AuxillerySpineTangent = false
  BaseFeature = -> Pocket020
  Binormal = (0,0,0)
  Mode = 0
  Profile = -> Sketch033
  Refine = true
  Spine = -> Sketch006 [Edge21,Edge20,Edge19,Edge34,Edge33,Edge32,Edge31,Edge30,Edge29,Edge28,Edge27,Edge26,Edge25,Edge24,Edge23,Edge22]
  SpineTangent = false
  Suppressed = false
  Transformation = 0
  Transition = 0
FEATURE [Sketcher::SketchObject] Sketch043  label="cut_for_better_connection"
  ArcFitTolerance = 1e-06
  AttachmentSupport = -> [XZ_Plane065]
  ExternalTypes = [0]
  FullyConstrained = true
  MakeInternals = false
  MapMode = 5
  Placement = pos=(0,0,0) rot=(1,0,0;1.5708rad)
  expr: Constraints[10] = 2 * VarSet.Base_connector_bounting_box_height
  expr: Constraints[12] = VarSet.case_height / 2
  expr: Constraints[9] = VarSet.Base_connector_internal_lug + 10 * VarSet.Base_connector_lug_offset
  sketch-geometry (6):
    g0: LineSegment StartX=-6.5 StartY=9.5 StartZ=0 EndX=-6.5 EndY=-34.5 EndZ=0
    g1: LineSegment StartX=-6.5 StartY=-34.5 StartZ=0 EndX=6.5 EndY=-34.5 EndZ=0
    g2: LineSegment StartX=6.5 StartY=-34.5 StartZ=0 EndX=6.5 EndY=9.5 EndZ=0
    g3: LineSegment StartX=6.5 StartY=9.5 StartZ=0 EndX=-6.5 EndY=9.5 EndZ=0
    g4: GeomPoint [constr] X=0 Y=-12.5 Z=0
    g5: GeomPoint X=0 Y=-12.5 Z=0
  constraints (14):
    c: Coincident(g0,g1)
    c: Coincident(g1,g2)
    c: Coincident(g2,g3)
    c: Coincident(g3,g0)
    c: Vertical(g0)
    c: Vertical(g2)
    c: Horizontal(g1)
    c: Horizontal(g3)
    c: Symmetric(g2,g0,g4)
    c: DistanceX(g0,g2) = 13
    c: DistanceY(g0,g0) = 44
    c: PointOnObject(g5,g-2)
    c: DistanceY(g5,g-1) = 12.5
    c: Coincident(g4,g5)
FEATURE [PartDesign::Pocket] Pocket027
  BaseFeature = -> Pocket016
  Direction = (0,1,-2e-16)
  Length = 12
  Length2 = 5
  Placement = pos=(0,0,0) rot=(1,0,0;1.5708rad)
  Profile = -> Sketch043
  ReferenceAxis = -> Sketch043 [N_Axis]
  Refine = true
  Reversed = true
  Suppressed = false
  Type = 0
  expr: Length = VarSet.Base_connector_height_lug
FEATURE [Sketcher::SketchObject] Sketch048  label="outside_clips"
  ArcFitTolerance = 1e-06
  AttachmentSupport = -> [XZ_Plane065]
  ExternalGeometry = -> [Pocket027]
  ExternalTypes = [0,0,0]
  FullyConstrained = true
  MakeInternals = false
  MapMode = 5
  Placement = pos=(0,0,0) rot=(1,0,0;1.5708rad)
  expr: Constraints[22] = VarSet.Base_connector_clip
  sketch-geometry (15):
    g0: GeomPoint X=-32.5 Y=-12.5 Z=0
    g1: GeomPoint X=32.5 Y=-12.5 Z=0
    g2: LineSegment [constr] StartX=-32.5 StartY=-12.5 StartZ=0 EndX=32.5 EndY=-12.5 EndZ=0
    g3: LineSegment StartX=-31.5 StartY=-8.5 StartZ=0 EndX=-31.5 EndY=-16.5 EndZ=0
    g4: LineSegment StartX=-31.5 StartY=-16.5 StartZ=0 EndX=-23.5 EndY=-16.5 EndZ=0
    g5: LineSegment StartX=-23.5 StartY=-16.5 StartZ=0 EndX=-23.5 EndY=-8.5 EndZ=0
    g6: LineSegment StartX=-23.5 StartY=-8.5 StartZ=0 EndX=-31.5 EndY=-8.5 EndZ=0
    g7: GeomPoint [constr] X=-27.5 Y=-12.5 Z=0
    g8: LineSegment StartX=23.5 StartY=-8.5 StartZ=0 EndX=23.5 EndY=-16.5 EndZ=0
    g9: LineSegment StartX=23.5 StartY=-16.5 StartZ=0 EndX=31.5 EndY=-16.5 EndZ=0
    g10: LineSegment StartX=31.5 StartY=-16.5 StartZ=0 EndX=31.5 EndY=-8.5 EndZ=0
    g11: LineSegment StartX=31.5 StartY=-8.5 StartZ=0 EndX=23.5 EndY=-8.5 EndZ=0
    g12: GeomPoint [constr] X=27.5 Y=-12.5 Z=0
    g13: GeomPoint [constr] X=-27.5 Y=-12.5 Z=0
    g14: GeomPoint [constr] X=27.5 Y=-12.5 Z=0
  constraints (31):
    c: Symmetric(g-6,g-6,g0)
    c: Symmetric(g-15,g-15,g1)
    c: Coincident(g2,g0)
    c: Coincident(g2,g1)
    c: Coincident(g3,g4)
    c: Coincident(g4,g5)
    c: Coincident(g5,g6)
    c: Coincident(g6,g3)
    c: Vertical(g3)
    c: Vertical(g5)
    c: Horizontal(g4)
    c: Horizontal(g6)
    c: Symmetric(g5,g3,g7)
    c: PointOnObject(g7,g2)
    c: Coincident(g8,g9)
    c: Coincident(g9,g10)
    c: Coincident(g10,g11)
    c: Coincident(g11,g8)
    c: Vertical(g8)
    c: Vertical(g10)
    c: Horizontal(g9)
    c: Symmetric(g10,g8,g12)
    c: DistanceX(g3,g5) = 8
    c: Equal(g6,g3)
    c: Equal(g3,g8)
    c: Equal(g8,g11)
    c: DistanceX(g0,g7) = 5
    c: Symmetric(g7,g12,g-2)
    c: Coincident(g13,g7)
    c: Coincident(g14,g12)
    c: Perpendicular(g10,g11)
FEATURE [Sketcher::SketchObject] Sketch049  label="inside_clips"
  ArcFitTolerance = 1e-06
  AttachmentOffset = pos=(0,0,1.6) rot=(0,0,1;0rad)
  AttachmentSupport = -> [XZ_Plane065]
  ExternalGeometry = -> [Sketch048]
  ExternalTypes = [0,0,0,0,0,0,0,0]
  FullyConstrained = true
  MakeInternals = false
  MapMode = 5
  Placement = pos=(0,-1.6,4e-16) rot=(1,0,0;1.5708rad)
  expr: .AttachmentOffset.Base.z = VarSet.Base_connector_clip_height
  expr: Constraints[27] = VarSet.Base_connector_clip * 0.5
  sketch-geometry (14):
    g0: LineSegment [constr] StartX=-31.5 StartY=-16.5 StartZ=0 EndX=-23.5 EndY=-8.5 EndZ=0
    g1: LineSegment [constr] StartX=23.5 StartY=-8.5 StartZ=0 EndX=31.5 EndY=-16.5 EndZ=0
    g2: GeomPoint X=-27.5 Y=-12.5 Z=0
    g3: GeomPoint X=27.5 Y=-12.5 Z=0
    g4: LineSegment StartX=-29.5 StartY=-10.5 StartZ=0 EndX=-29.5 EndY=-14.5 EndZ=0
    g5: LineSegment StartX=-29.5 StartY=-14.5 StartZ=0 EndX=-25.5 EndY=-14.5 EndZ=0
    g6: LineSegment StartX=-25.5 StartY=-14.5 StartZ=0 EndX=-25.5 EndY=-10.5 EndZ=0
    g7: LineSegment StartX=-25.5 StartY=-10.5 StartZ=0 EndX=-29.5 EndY=-10.5 EndZ=0
    g8: GeomPoint [constr] X=-27.5 Y=-12.5 Z=0
    g9: LineSegment StartX=25.5 StartY=-10.5 StartZ=0 EndX=25.5 EndY=-14.5 EndZ=0
    g10: LineSegment StartX=25.5 StartY=-14.5 StartZ=0 EndX=29.5 EndY=-14.5 EndZ=0
    g11: LineSegment StartX=29.5 StartY=-14.5 StartZ=0 EndX=29.5 EndY=-10.5 EndZ=0
    g12: LineSegment StartX=29.5 StartY=-10.5 StartZ=0 EndX=25.5 EndY=-10.5 EndZ=0
    g13: GeomPoint [constr] X=27.5 Y=-12.5 Z=0
  constraints (30):
    c: Coincident(g0,g-4)
    c: Coincident(g0,g-6)
    c: Coincident(g1,g-8)
    c: Coincident(g1,g-10)
    c: Symmetric(g0,g0,g2)
    c: Symmetric(g1,g1,g3)
    c: Coincident(g4,g5)
    c: Coincident(g5,g6)
    c: Coincident(g6,g7)
    c: Coincident(g7,g4)
    c: Vertical(g4)
    c: Vertical(g6)
    c: Horizontal(g5)
    c: Horizontal(g7)
    c: Symmetric(g6,g4,g8)
    c: Coincident(g8,g2)
    c: Coincident(g9,g10)
    c: Coincident(g10,g11)
    c: Coincident(g11,g12)
    c: Coincident(g12,g9)
    c: Vertical(g9)
    c: Vertical(g11)
    c: Horizontal(g10)
    c: Horizontal(g12)
    c: Symmetric(g11,g9,g13)
    c: Coincident(g13,g3)
    c: PointOnObject(g10,g1)
    c: DistanceX(g4,g6) = 4
    c: Equal(g7,g4)
    c: Equal(g4,g12)
FEATURE [PartDesign::AdditiveLoft] AdditiveLoft  label="clips"
  BaseFeature = -> Pocket027
  Closed = false
  Placement = pos=(0,0,0) rot=(1,0,0;1.5708rad)
  Profile = -> Sketch048
  Refine = true
  Ruled = false
  Sections = -> [Sketch049]
  Suppressed = false
FEATURE [Sketcher::SketchObject] Sketch053  label="oring_diameer"
  ArcFitTolerance = 1e-06
  AttachmentSupport = -> [XZ_Plane065]
  ExternalGeometry = -> [Sketch011]
  ExternalTypes = [0]
  FullyConstrained = true
  MakeInternals = false
  MapMode = 5
  Placement = pos=(0,0,0) rot=(1,0,0;1.5708rad)
  expr: Constraints[1] = VarSet.Base_connector_oring_outside_diameter - VarSet.Base_connector_oring_cross_section
  sketch-geometry (1):
    g0: Circle CenterX=0 CenterY=-12.5 CenterZ=0 NormalX=0 NormalY=0 NormalZ=1 AngleXU=0 Radius=9.5
  constraints (2):
    c: Coincident(g0,g-3)
    c: Diameter(g0) = 19
FEATURE [Sketcher::SketchObject] Sketch060  label="cross_section001"
  ArcFitTolerance = 1e-06
  AttachmentSupport = -> [YZ_Plane065]
  ExternalGeometry = -> [Sketch053]
  ExternalTypes = [0]
  FullyConstrained = true
  MakeInternals = false
  MapMode = 5
  Placement = pos=(0,0,0) rot=(0.57735,0.57735,0.57735;2.0944rad)
  expr: Constraints[0] = VarSet.Base_connector_oring_cross_section
  expr: Constraints[5] = VarSet.Base_connector_oring_offset
  sketch-geometry (2):
    g0: Circle CenterX=-0.2 CenterY=-3 CenterZ=0 NormalX=0 NormalY=0 NormalZ=1 AngleXU=0 Radius=1
    g1: LineSegment [constr] StartX=-5 StartY=-3 StartZ=0 EndX=5 EndY=-3 EndZ=0
  constraints (6):
    c: Diameter(g0) = 2
    c: Distance(g1) = 10
    c: Symmetric(g1,g1,g-2)
    c: PointOnObject(g0,g1)
    c: PointOnObject(g-3,g1)
    c: DistanceX(g0,g-3) = 0.2
FEATURE [PartDesign::SubtractivePipe] SubtractivePipe005  label="oring_grove"
  AuxilleryCurvelinear = true
  AuxillerySpineTangent = false
  BaseFeature = -> AdditiveLoft
  Binormal = (0,0,0)
  Mode = 0
  Placement = pos=(0,0,0) rot=(1,0,0;1.5708rad)
  Profile = -> Sketch060
  Refine = true
  Spine = -> Sketch053
  SpineTangent = false
  Suppressed = false
  Transformation = 0
  Transition = 0
FEATURE [PartDesign::Fillet] Fillet002
  Base = -> SubtractivePipe005 [Edge67,Edge71,Edge60,Edge58,Edge65,Edge63,Edge62,Edge69,Edge51,Edge57]
  BaseFeature = -> SubtractivePipe005
  Placement = pos=(0,0,0) rot=(1,0,0;1.5708rad)
  Radius = 1
  Refine = true
  SupportTransform = false
  Suppressed = false
  UseAllEdges = false
FEATURE [PartDesign::Body] Body005  label="battery_connector"
  AllowCompound = false
  Group = -> [Sketch011,Pad008,Pad009,Sketch012,Pocket012,Sketch018,Pocket016,Sketch043,Pocket027,Sketch048,Sketch049,AdditiveLoft,Sketch053,Sketch060,SubtractivePipe005,Fillet002]
  Origin = -> Origin131
  Placement = pos=(0,-1.5,0) rot=(0,0,1;0rad)
  Tip = -> Fillet002
  expr: .Placement.Base.y = -1 * VarSet.Base_pogopin_cutout_height
FEATURE [Sketcher::SketchObject] Sketch061  label="pogopins001"
  ArcFitTolerance = 1e-06
  ExternalTypes = [0]
  FullyConstrained = true
  MakeInternals = false
  MapMode = 5
  Placement = pos=(0,0,0) rot=(1,0,0;1.5708rad)
  expr: Constraints[10] = VarSet.case_height / 2
  expr: Constraints[11] = VarSet.Base_pogoping_lenght
  expr: Constraints[12] = 2 * VarSet.Base_pogopins_r
  sketch-geometry (7):
    g0: LineSegment [constr] StartX=-7.55 StartY=-10.4 StartZ=0 EndX=-7.55 EndY=-14.6 EndZ=0
    g1: LineSegment StartX=-7.55 StartY=-14.6 StartZ=0 EndX=7.55 EndY=-14.6 EndZ=0
    g2: LineSegment [constr] StartX=7.55 StartY=-14.6 StartZ=0 EndX=7.55 EndY=-10.4 EndZ=0
    g3: LineSegment StartX=7.55 StartY=-10.4 StartZ=0 EndX=-7.55 EndY=-10.4 EndZ=0
    g4: GeomPoint [constr] X=0 Y=-12.5 Z=0
    g5: ArcOfCircle CenterX=7.55 CenterY=-12.5 CenterZ=0 NormalX=0 NormalY=0 NormalZ=1 AngleXU=0 Radius=2.1 StartAngle=4.71239 EndAngle=7.85398
    g6: ArcOfCircle CenterX=-7.55 CenterY=-12.5 CenterZ=0 NormalX=0 NormalY=0 NormalZ=1 AngleXU=0 Radius=2.1 StartAngle=1.5708 EndAngle=4.71239
  constraints (19):
    c: Coincident(g0,g1)
    c: Coincident(g1,g2)
    c: Coincident(g2,g3)
    c: Coincident(g3,g0)
    c: Vertical(g0)
    c: Vertical(g2)
    c: Horizontal(g1)
    c: Horizontal(g3)
    c: Symmetric(g2,g0,g4)
    c: PointOnObject(g4,g-2)
    c: DistanceY(g4,g-1) = 12.5
    c: Distance(g0,g2) = 15.1
    c: DistanceY(g1,g2) = 4.2
    c: Symmetric(g0,g0,g6)
    c: Coincident(g6,g0)
    c: Coincident(g6,g0)
    c: Coincident(g5,g1)
    c: Coincident(g5,g2)
    c: PointOnObject(g5,g2)
FEATURE [Sketcher::SketchObject] Sketch062  label="nuts001"
  ArcFitTolerance = 1e-06
  AttachmentOffset = pos=(0,0,-25) rot=(0,0,1;0rad)
  AttachmentSupport = -> [XY_Plane058]
  ExternalTypes = [0]
  FullyConstrained = true
  MakeInternals = false
  MapMode = 5
  Placement = pos=(0,0,-25) rot=(0,0,1;0rad)
  expr: .AttachmentOffset.Base.z = -1 * VarSet.case_height
  expr: Constraints[10] = VarSet.Base_battery_lenght - 2 * 3.6 mm
  expr: Constraints[8] = VarSet.base_width - 2 * 3.6 mm
  sketch-geometry (32):
    g0: LineSegment [constr] StartX=-28.9 StartY=81.4 StartZ=0 EndX=-28.9 EndY=3.6 EndZ=0
    g1: LineSegment [constr] StartX=-28.9 StartY=3.6 StartZ=0 EndX=28.9 EndY=3.6 EndZ=0
    g2: LineSegment [constr] StartX=28.9 StartY=3.6 StartZ=0 EndX=28.9 EndY=81.4 EndZ=0
    g3: LineSegment [constr] StartX=28.9 StartY=81.4 StartZ=0 EndX=-28.9 EndY=81.4 EndZ=0
    g4: LineSegment StartX=-25.7246 StartY=81.4 StartZ=0 EndX=-27.3123 EndY=84.15 EndZ=0
    g5: LineSegment StartX=-27.3123 StartY=84.15 StartZ=0 EndX=-30.4877 EndY=84.15 EndZ=0
    g6: LineSegment StartX=-30.4877 StartY=84.15 StartZ=0 EndX=-32.0754 EndY=81.4 EndZ=0
    g7: LineSegment StartX=-32.0754 StartY=81.4 StartZ=0 EndX=-30.4877 EndY=78.65 EndZ=0
    g8: LineSegment StartX=-30.4877 StartY=78.65 StartZ=0 EndX=-27.3123 EndY=78.65 EndZ=0
    g9: LineSegment StartX=-27.3123 StartY=78.65 StartZ=0 EndX=-25.7246 EndY=81.4 EndZ=0
    g10: Circle [constr] CenterX=-28.9 CenterY=81.4 CenterZ=0 NormalX=0 NormalY=0 NormalZ=1 AngleXU=0 Radius=3.17543
    g11: LineSegment StartX=32.0754 StartY=81.4 StartZ=0 EndX=30.4877 EndY=84.15 EndZ=0
    g12: LineSegment StartX=30.4877 StartY=84.15 StartZ=0 EndX=27.3123 EndY=84.15 EndZ=0
    g13: LineSegment StartX=27.3123 StartY=84.15 StartZ=0 EndX=25.7246 EndY=81.4 EndZ=0
    g14: LineSegment StartX=25.7246 StartY=81.4 StartZ=0 EndX=27.3123 EndY=78.65 EndZ=0
    g15: LineSegment StartX=27.3123 StartY=78.65 StartZ=0 EndX=30.4877 EndY=78.65 EndZ=0
    g16: LineSegment StartX=30.4877 StartY=78.65 StartZ=0 EndX=32.0754 EndY=81.4 EndZ=0
    g17: Circle [constr] CenterX=28.9 CenterY=81.4 CenterZ=0 NormalX=0 NormalY=0 NormalZ=1 AngleXU=0 Radius=3.17543
    g18: LineSegment StartX=30.4877 StartY=6.35 StartZ=0 EndX=27.3123 EndY=6.35 EndZ=0
    g19: LineSegment StartX=27.3123 StartY=6.35 StartZ=0 EndX=25.7246 EndY=3.6 EndZ=0
    g20: LineSegment StartX=25.7246 StartY=3.6 StartZ=0 EndX=27.3123 EndY=0.85 EndZ=0
    g21: LineSegment StartX=27.3123 StartY=0.85 StartZ=0 EndX=30.4877 EndY=0.85 EndZ=0
    g22: LineSegment StartX=30.4877 StartY=0.85 StartZ=0 EndX=32.0754 EndY=3.6 EndZ=0
    g23: LineSegment StartX=32.0754 StartY=3.6 StartZ=0 EndX=30.4877 EndY=6.35 EndZ=0
    g24: Circle [constr] CenterX=28.9 CenterY=3.6 CenterZ=0 NormalX=0 NormalY=0 NormalZ=1 AngleXU=0 Radius=3.17543
    g25: LineSegment StartX=-30.4877 StartY=0.85 StartZ=0 EndX=-27.3123 EndY=0.85 EndZ=0
    g26: LineSegment StartX=-27.3123 StartY=0.85 StartZ=0 EndX=-25.7246 EndY=3.6 EndZ=0
    g27: LineSegment StartX=-25.7246 StartY=3.6 StartZ=0 EndX=-27.3123 EndY=6.35 EndZ=0
    g28: LineSegment StartX=-27.3123 StartY=6.35 StartZ=0 EndX=-30.4877 EndY=6.35 EndZ=0
    g29: LineSegment StartX=-30.4877 StartY=6.35 StartZ=0 EndX=-32.0754 EndY=3.6 EndZ=0
    g30: LineSegment StartX=-32.0754 StartY=3.6 StartZ=0 EndX=-30.4877 EndY=0.85 EndZ=0
    g31: Circle [constr] CenterX=-28.9 CenterY=3.6 CenterZ=0 NormalX=0 NormalY=0 NormalZ=1 AngleXU=0 Radius=3.17543
  constraints (75):
    c: Coincident(g0,g1)
    c: Coincident(g1,g2)
    c: Coincident(g2,g3)
    c: Coincident(g3,g0)
    c: Vertical(g0)
    c: Vertical(g2)
    c: Horizontal(g1)
    c: Symmetric(g0,g2,g-2)
    c: DistanceX(g0,g2) = 57.8
    c: Distance(g1,g-1) = 3.6
    c: DistanceY(g1,g2) = 77.8
    c: Coincident(g4,g5)
    c: Coincident(g5,g6)
    c: Coincident(g6,g7)
    c: Coincident(g7,g8)
    c: Coincident(g8,g9)
    c: Coincident(g9,g4)
    c: Equal(g4, g5-g9) x5
    c: PointOnObject(g4,g10)
    c: PointOnObject(g5,g10)
    c: PointOnObject(g6,g10)
    c: PointOnObject(g7,g10)
    c: PointOnObject(g8,g10)
    c: PointOnObject(g9,g10)
    c: Coincident(g10,g0)
    c: PointOnObject(g9,g3)
    c: Coincident(g11,g12)
    c: Coincident(g12,g13)
    c: Coincident(g13,g14)
    c: Coincident(g14,g15)
    c: Coincident(g15,g16)
    c: Coincident(g16,g11)
    c: Equal(g11, g12-g16) x5
    c: PointOnObject(g11,g17)
    c: PointOnObject(g12,g17)
    c: PointOnObject(g13,g17)
    c: PointOnObject(g14,g17)
    c: PointOnObject(g15,g17)
    c: PointOnObject(g16,g17)
    c: Coincident(g17,g2)
    c: Coincident(g18,g19)
    c: Coincident(g19,g20)
    c: Coincident(g20,g21)
    c: Coincident(g21,g22)
    c: Coincident(g22,g23)
    c: Coincident(g23,g18)
    c: Equal(g18, g19-g23) x5
    c: PointOnObject(g18,g24)
    c: PointOnObject(g19,g24)
    c: PointOnObject(g20,g24)
    c: PointOnObject(g21,g24)
    c: PointOnObject(g22,g24)
    c: PointOnObject(g23,g24)
    c: Coincident(g24,g1)
    c: Coincident(g25,g26)
    c: Coincident(g26,g27)
    c: Coincident(g27,g28)
    c: Coincident(g28,g29)
    c: Coincident(g29,g30)
    c: Coincident(g30,g25)
    c: Equal(g25, g26-g30) x5
    c: PointOnObject(g25,g31)
    c: PointOnObject(g26,g31)
    c: PointOnObject(g27,g31)
    c: PointOnObject(g28,g31)
    c: PointOnObject(g29,g31)
    c: PointOnObject(g30,g31)
    c: Parallel(g-1,g21)
    c: Parallel(g15,g-1)
    c: Equal(g10,g17)
    c: Equal(g31,g24)
    c: DistanceY(g7,g5) = 5.5
    c: Coincident(g31,g0)
    c: Parallel(g25,g-1)
    c: Equal(g10,g31)
FEATURE [PartDesign::Pocket] Pocket030  label="nuts_"
  BaseFeature = -> SubtractivePipe001
  Direction = (0,0,-1)
  Length = 20
  Length2 = 5
  Midplane = true
  Profile = -> Sketch062
  ReferenceAxis = -> Sketch062 [N_Axis]
  Refine = true
  Suppressed = false
  Type = 0
  expr: Length = VarSet.case_height * 0.8
FEATURE [PartDesign::LinearPattern] LinearPattern
  BaseFeature = -> Pocket030
  Direction = -> Sketch007 [N_Axis]
  Length = 50
  Mode = 0
  Occurrences = 3
  Offset = 25
  Originals = -> [Pad005]
  Refine = true
  Reversed = true
  Suppressed = false
  TransformMode = 0
FEATURE [PartDesign::Body] Body002  label="battery_body"
  AllowCompound = false
  Group = -> [Sketch006,Pad004,Pocket005,Pocket006,Sketch007,Pad005,Sketch022,Pocket020,Sketch033,SubtractivePipe001,Sketch061,Sketch062,Pocket030,LinearPattern]
  Origin = -> Origin116
  Tip = -> LinearPattern
COMPONENT P10 — recipe-attached ("battery_cover002", modeled in this document).
Construction recipe (the document's own serialized feature program — sketch geometry with constraints, then the solid features built on it; lengths are millimeters unless a unit is written):

FEATURE [Sketcher::SketchObject] Sketch030
  ArcFitTolerance = 1e-06
  AttachmentSupport = -> [XY_Plane075]
  ExternalTypes = [0]
  FullyConstrained = true
  MakeInternals = false
  MapMode = 5
  expr: Constraints[7] = VarSet.base_width
  expr: Constraints[8] = VarSet.Base_battery_lenght
  sketch-geometry (8):
    g0: LineSegment StartX=-32.5 StartY=0 StartZ=0 EndX=32.5 EndY=0 EndZ=0
    g1: LineSegment StartX=32.5 StartY=0 StartZ=0 EndX=32.5 EndY=81 EndZ=0
    g2: LineSegment StartX=28.5 StartY=85 StartZ=0 EndX=-28.5 EndY=85 EndZ=0
    g3: LineSegment StartX=-32.5 StartY=81 StartZ=0 EndX=-32.5 EndY=0 EndZ=0
    g4: ArcOfCircle CenterX=-28.5 CenterY=81 CenterZ=0 NormalX=0 NormalY=0 NormalZ=1 AngleXU=0 Radius=4 StartAngle=1.5708 EndAngle=3.14159
    g5: GeomPoint [constr] X=-32.5 Y=85 Z=0
    g6: ArcOfCircle CenterX=28.5 CenterY=81 CenterZ=0 NormalX=0 NormalY=0 NormalZ=1 AngleXU=0 Radius=4 StartAngle=4.08e-14 EndAngle=1.5708
    g7: GeomPoint [constr] X=32.5 Y=85 Z=0
  constraints (19):
    c: Coincident(g0,g1)
    c: Coincident(g3,g0)
    c: Horizontal(g0)
    c: Vertical(g1)
    c: Vertical(g3)
    c: PointOnObject(g0,g-1)
    c: Symmetric(g5,g7,g-2)
    c: DistanceX(g5,g7) = 65
    c: DistanceY(g0,g7) = 85
    c: PointOnObject(g5,g3)
    c: PointOnObject(g5,g2)
    c: Tangent(g3,g4) = -1.5708
    c: Tangent(g2,g4) = -1.5708
    c: PointOnObject(g7,g2)
    c: PointOnObject(g7,g1)
    c: Tangent(g2,g6) = -1.5708
    c: Tangent(g1,g6) = -1.5708
    c: Equal(g4,g6)
    c: Radius(g4) = 4
FEATURE [PartDesign::SubShapeBinder] Binder003
  BindCopyOnChange = 0
  BindMode = 0
  ClaimChildren = false
  Context = -> Part006 [Body011.Binder003.]
  Fuse = false
  MakeFace = true
  OffsetFill = false
  OffsetIntersection = false
  OffsetJoinType = 0
  OffsetOpenResult = false
  PartialLoad = false
  Refine = true
  Relative = true
  Support = -> [Part002[Body002.Sketch006.]]
  _Version = 2
FEATURE [PartDesign::Pad] Pad013
  Direction = (0,0,1)
  Length = 5
  Length2 = 10
  Profile = -> Sketch030
  ReferenceAxis = -> Sketch030 [N_Axis]
  Refine = true
  Reversed = true
  Suppressed = false
  Type = 0
  expr: Length = VarSet.Base_lid_thickness
FEATURE [Sketcher::SketchObject] Sketch036
  ArcFitTolerance = 1e-06
  AttachmentSupport = -> [Pad013]
  ExternalGeometry = -> [Binder003]
  ExternalTypes = [0,0,0,0]
  FullyConstrained = true
  MakeInternals = false
  MapMode = 5
  Placement = pos=(0,0,-5) rot=(1,0,0;3.14159rad)
FEATURE [PartDesign::Hole] Hole001
  BaseFeature = -> Pad013
  CustomThreadClearance = 0
  Depth = 25
  DepthType = 0
  Diameter = 3.2
  DrillForDepth = false
  DrillPoint = 1
  DrillPointAngle = 118
  HoleCutCountersinkAngle = 90
  HoleCutCustomValues = false
  HoleCutDepth = 0
  HoleCutDiameter = 6.1
  HoleCutType = 2
  ModelThread = false
  Profile = -> Sketch036
  Refine = true
  Suppressed = false
  Tapered = false
  TaperedAngle = 90
  ThreadClass = 0
  ThreadDepth = 25
  ThreadDepthType = 0
  ThreadDirection = 0
  ThreadFit = 1
  ThreadSize = 9
  ThreadType = 1
  Threaded = false
  UseCustomThreadClearance = false
FEATURE [Sketcher::SketchObject] Sketch037  label="grasket_outside"
  ArcFitTolerance = 1e-06
  AttachmentSupport = -> [XY_Plane075]
  ExternalGeometry = -> [Binder003]
  ExternalTypes = [0,0,0,0,0,0,0,0,0,0,0,0,0,0,0,0,0,0]
  FullyConstrained = true
  MakeInternals = false
  MapMode = 5
FEATURE [Sketcher::SketchObject] Sketch038
  ArcFitTolerance = 1e-06
  AttachmentSupport = -> [YZ_Plane075]
  ExternalGeometry = -> [Binder003]
  ExternalTypes = [0]
  FullyConstrained = true
  MakeInternals = false
  MapMode = 5
  Placement = pos=(0,0,0) rot=(0.57735,0.57735,0.57735;2.0944rad)
  expr: Constraints[10] = VarSet.Base_gasket_width
  expr: Constraints[11] = VarSet.Base_gasket_height
  sketch-geometry (5):
    g0: LineSegment StartX=1 StartY=1 StartZ=0 EndX=1 EndY=-1 EndZ=0
    g1: LineSegment StartX=1 StartY=-1 StartZ=0 EndX=2 EndY=-1 EndZ=0
    g2: LineSegment StartX=2 StartY=-1 StartZ=0 EndX=2 EndY=1 EndZ=0
    g3: LineSegment StartX=2 StartY=1 StartZ=0 EndX=1 EndY=1 EndZ=0
    g4: GeomPoint [constr] X=1.5 Y=0 Z=0
  constraints (12):
    c: Coincident(g0,g1)
    c: Coincident(g1,g2)
    c: Coincident(g2,g3)
    c: Coincident(g3,g0)
    c: Vertical(g0)
    c: Vertical(g2)
    c: Horizontal(g1)
    c: Horizontal(g3)
    c: Symmetric(g2,g0,g4)
    c: Coincident(g4,g-3)
    c: DistanceX(g0,g2) = 1
    c: DistanceY(g0,g0) = 2
FEATURE [Sketcher::SketchObject] Sketch039
  ArcFitTolerance = 1e-06
  AttachmentSupport = -> [XY_Plane075]
  ExternalGeometry = -> [Binder003]
  ExternalTypes = [0,0,0,0,0,0,0,0]
  FullyConstrained = true
  MakeInternals = false
  MapMode = 5
FEATURE [PartDesign::SubtractivePipe] SubtractivePipe003
  AuxilleryCurvelinear = true
  AuxillerySpineTangent = false
  BaseFeature = -> Hole001
  Binormal = (0,0,0)
  Mode = 0
  Profile = -> Sketch038
  Refine = true
  Spine = -> Sketch037 [Edge7,Edge6,Edge5,Edge4,Edge3,Edge2,Edge1,Edge16,Edge15,Edge14,Edge13,Edge12,Edge11,Edge10,Edge9,Edge8]
  SpineTangent = false
  Suppressed = false
  Transformation = 0
  Transition = 0
FEATURE [PartDesign::Fillet] Fillet004
  Base = -> SubtractivePipe003 [Edge4,Edge10,Edge7,Edge35,Edge36,Edge34]
  BaseFeature = -> SubtractivePipe003
  Radius = 1
  Refine = true
  SupportTransform = false
  Suppressed = false
  UseAllEdges = false
FEATURE [PartDesign::Pocket] Pocket033
  BaseFeature = -> Fillet004
  Direction = (0,0,-1)
  Length = 0.6
  Length2 = 5
  Profile = -> Sketch039
  ReferenceAxis = -> Sketch039 [N_Axis]
  Refine = true
  Suppressed = false
  Type = 0
  expr: Length = 0.2 * VarSet.Base_case_thickness
FEATURE [PartDesign::Body] Body011  label="battery_cover001"
  AllowCompound = false
  Group = -> [Sketch030,Binder003,Pad013,Sketch036,Hole001,Sketch037,Sketch038,SubtractivePipe003,Sketch039,Fillet004,Pocket033]
  Origin = -> Origin151
  Tip = -> Pocket033
COMPONENT P11 — recipe-attached ("battery_cover_gasket002", modeled in this document).
Construction recipe (the document's own serialized feature program — sketch geometry with constraints, then the solid features built on it; lengths are millimeters unless a unit is written):

FEATURE [PartDesign::SubShapeBinder] Binder004
  BindCopyOnChange = 0
  BindMode = 0
  ClaimChildren = false
  Context = -> Part005 [Body010.Binder004.]
  Fuse = false
  MakeFace = true
  OffsetFill = false
  OffsetIntersection = false
  OffsetJoinType = 0
  OffsetOpenResult = false
  PartialLoad = false
  Refine = true
  Relative = true
  Support = -> [Part002[Body002.Sketch006.]]
  _Version = 2
FEATURE [Sketcher::SketchObject] Sketch040  label="line"
  ArcFitTolerance = 1e-06
  AttachmentSupport = -> [XY_Plane073]
  ExternalGeometry = -> [Binder004]
  ExternalTypes = [0,0,0,0,0,0,0,0,0,0,0,0,0,0,0,0]
  FullyConstrained = true
  MakeInternals = false
  MapMode = 5
FEATURE [Sketcher::SketchObject] Sketch070  label="profile002"
  ArcFitTolerance = 1e-06
  AttachmentSupport = -> [YZ_Plane073]
  ExternalGeometry = -> [Sketch040]
  ExternalTypes = [0]
  FullyConstrained = true
  MakeInternals = false
  MapMode = 5
  Placement = pos=(0,0,0) rot=(0.57735,0.57735,0.57735;2.0944rad)
  expr: Constraints[10] = VarSet.Base_gasket_width
  expr: Constraints[11] = VarSet.Base_gasket_height
  sketch-geometry (5):
    g0: LineSegment StartX=1 StartY=1 StartZ=0 EndX=1 EndY=-1 EndZ=0
    g1: LineSegment StartX=1 StartY=-1 StartZ=0 EndX=2 EndY=-1 EndZ=0
    g2: LineSegment StartX=2 StartY=-1 StartZ=0 EndX=2 EndY=1 EndZ=0
    g3: LineSegment StartX=2 StartY=1 StartZ=0 EndX=1 EndY=1 EndZ=0
    g4: GeomPoint [constr] X=1.5 Y=-1e-16 Z=0
  constraints (12):
    c: Coincident(g0,g1)
    c: Coincident(g1,g2)
    c: Coincident(g2,g3)
    c: Coincident(g3,g0)
    c: Vertical(g0)
    c: Vertical(g2)
    c: Horizontal(g1)
    c: Horizontal(g3)
    c: Symmetric(g2,g0,g4)
    c: Coincident(g4,g-3)
    c: Distance(g3,g3) = 1
    c: Distance(g0,g0) = 2
FEATURE [PartDesign::AdditivePipe] AdditivePipe001
  AuxilleryCurvelinear = true
  AuxillerySpineTangent = false
  Binormal = (0,0,0)
  Mode = 0
  Placement = pos=(0,0,0) rot=(1,1,1;2.0944rad)
  Profile = -> Sketch070
  Refine = true
  Spine = -> Sketch040 [Edge1,Edge16,Edge15,Edge14,Edge13,Edge12,Edge11,Edge10,Edge9,Edge8,Edge7,Edge6,Edge5,Edge4,Edge3,Edge2]
  SpineTangent = false
  Suppressed = false
  Transformation = 0
  Transition = 0
FEATURE [PartDesign::Body] Body010  label="battery_cover_gasket001"
  AllowCompound = false
  Group = -> [Binder004,Sketch040,Sketch070,AdditivePipe001]
  Origin = -> Origin147
  Tip = -> AdditivePipe001
